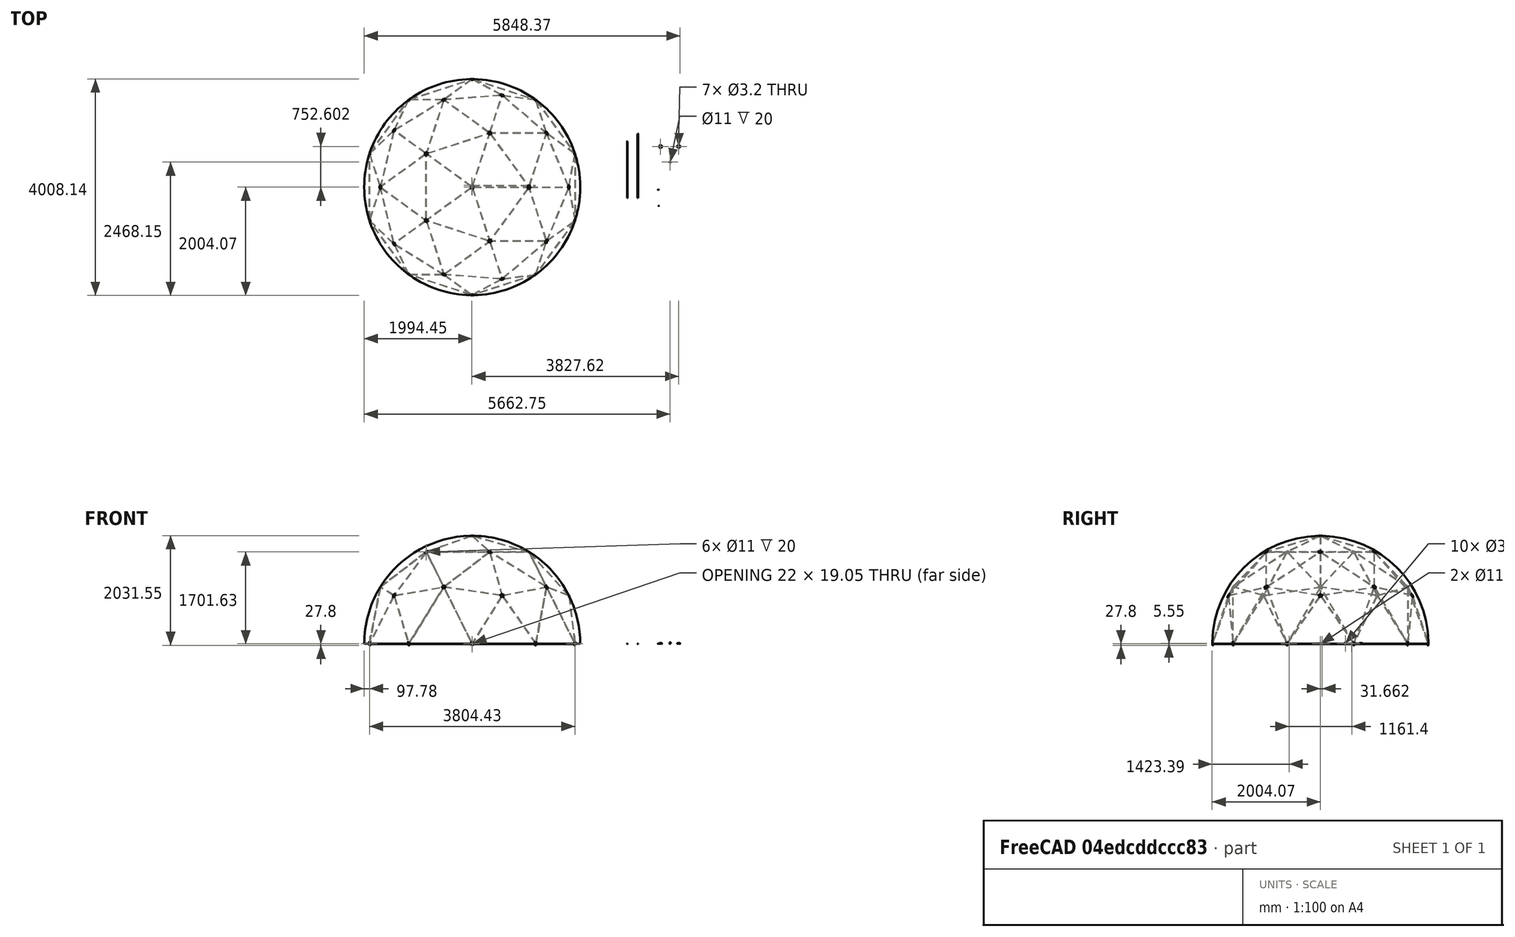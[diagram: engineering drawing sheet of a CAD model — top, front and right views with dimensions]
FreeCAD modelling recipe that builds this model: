
FCSTD DOCUMENT  (FreeCAD 0.20R29177 +233 (Git))
Label: 02-domo-3D
License: All rights reserved
LicenseURL: http://en.wikipedia.org/wiki/All_rights_reserved
objects: Part::Feature×235, Part::Part2DObjectPython×138, App::DocumentObjectGroup×21, App::Annotation×18, Part::Mirroring×7, App::FeaturePython×4, Part::Sphere×1, Part::Cylinder×1
note: 382 computed .brp shape members not serialized (recipe doc carries the construction recipe); baked Part::Feature solids carry a one-line shape summary decoded from their .brp

FEATURE [Part::Part2DObjectPython] Line  # Draft 2D object (typed FeaturePython)
  ChamferSize = 0
  Closed = false
  End = (-1902.16,617.998,0)
  FilletRadius = 0
  Length = 1236.1
  MakeFace = true
  MapMode = 5
  Placement = pos=(-1154.86,1595.54,0) rot=(0,0,-1;0.628319rad)
  Points = (2) [(-30,6,0),(-30,-1230.1,0)]
  Start = (-1175.6,1618.02,0)
  Subdivisions = 0
FEATURE [Part::Part2DObjectPython] Line003  # Draft 2D object (typed FeaturePython)
  ChamferSize = 0
  Closed = false
  End = (-1175.6,1618.02,0)
  FilletRadius = 0
  Length = 1236.1
  MakeFace = true
  MapMode = 5
  Placement = pos=(3.56417,1969.61,0) rot=(0,0,-1;1.25664rad)
  Points = (2) [(-30,6,0),(-30,-1230.1,0)]
  Start = (3.56741e-11,2000,0)
  Subdivisions = 0
FEATURE [Part::Mirroring] Part__Mirroring  label="Line (Mirror #1)"
  Base = (0,0,0)
  Normal = (1,0,0)
  Source = -> Line
FEATURE [Part::Mirroring] Part__Mirroring001  label="Line003 (Mirror #2)"
  Base = (0,0,0)
  Normal = (1,0,0)
  Source = -> Line003
FEATURE [Part::Mirroring] Part__Mirroring002  label="Line (Mirror #3)"
  Base = (0,0,0)
  Normal = (0,1,0)
  Source = -> Line
FEATURE [Part::Mirroring] Part__Mirroring003  label="Line003 (Mirror #4)"
  Base = (0,0,0)
  Normal = (0,1,0)
  Source = -> Line003
FEATURE [Part::Mirroring] Part__Mirroring004  label="Line (Mirror #5)"
  Base = (0,0,0)
  Normal = (0,1,0)
  Source = -> Part__Mirroring
FEATURE [Part::Mirroring] Part__Mirroring005  label="Line003 (Mirror #6)"
  Base = (0,0,0)
  Normal = (0,1,0)
  Source = -> Part__Mirroring001
FEATURE [Part::Part2DObjectPython] Line006  # Draft 2D object (typed FeaturePython)
  ChamferSize = 0
  Closed = false
  End = (-1902.16,-617.998,0)
  FilletRadius = 0
  Length = 1236
  MakeFace = true
  MapMode = 5
  Points = (2) [(-1902.16,617.998,0),(-1902.16,-617.998,0)]
  Start = (-1902.16,617.998,0)
  Subdivisions = 0
FEATURE [Part::Sphere] Sphere
  Angle1 = 0
  Angle2 = 90
  Angle3 = 360
  AttacherType = Attacher::AttachEngine3D
  Radius = 2000
FEATURE [Part::Part2DObjectPython] Line014  # Draft 2D object (typed FeaturePython)
  ChamferSize = 0
  Closed = false
  End = (1902.16,3e-10,0)
  FilletRadius = 0
  Length = 1902.16
  MakeFace = true
  MapMode = 5
  Points = (2) [(-1.99975e-10,3.00133e-10,0),(1902.16,3.0025e-10,0)]
  Start = (0,0,0)
  Subdivisions = 0
FEATURE [Part::Part2DObjectPython] Line015  # Draft 2D object (typed FeaturePython)
  ChamferSize = 0
  Closed = false
  End = (1902.16,3e-10,0)
  FilletRadius = 0
  Length = 1902.16
  MakeFace = true
  MapMode = 5
  Points = (2) [(-1.99975e-10,3.00133e-10,0),(1902.16,3.0025e-10,0)]
  Start = (0,0,0)
  Subdivisions = 0
FEATURE [Part::Part2DObjectPython] Line016  # Draft 2D object (typed FeaturePython)
  ChamferSize = 0
  Closed = false
  End = (587.785,1809.02,0)
  FilletRadius = 0
  Length = 1902.11
  MakeFace = true
  MapMode = 5
  Points = (2) [(-1.99975e-10,3.00133e-10,0),(587.785,1809.02,0)]
  Start = (0,0,0)
  Subdivisions = 0
FEATURE [Part::Part2DObjectPython] Line017  # Draft 2D object (typed FeaturePython)
  ChamferSize = 0
  Closed = false
  End = (-1538.86,1118.05,0)
  FilletRadius = 0
  Length = 1902.13
  MakeFace = true
  MapMode = 5
  Points = (2) [(-1.99975e-10,3.00133e-10,0),(-1538.86,1118.05,0)]
  Start = (0,0,0)
  Subdivisions = 0
FEATURE [Part::Part2DObjectPython] Line018  # Draft 2D object (typed FeaturePython)
  ChamferSize = 0
  Closed = false
  End = (-1538.86,-1118.05,0)
  FilletRadius = 0
  Length = 1902.13
  MakeFace = true
  MapMode = 5
  Points = (2) [(-1.99975e-10,3.00133e-10,0),(-1538.86,-1118.05,0)]
  Start = (0,0,0)
  Subdivisions = 0
FEATURE [Part::Part2DObjectPython] Line019  # Draft 2D object (typed FeaturePython)
  ChamferSize = 0
  Closed = false
  End = (-577.454,-703.099,0)
  FilletRadius = 0
  Length = 1093.1
  MakeFace = true
  MapMode = 5
  Placement = pos=(1075.61,-2380.95,0) rot=(0,0,-1;0.581932rad)
  Points = (2) [(-2300,-600,0),(-2303.19,493.095,0)]
  Start = (-1175.6,-1618.02,0)
  Subdivisions = 0
FEATURE [Part::Part2DObjectPython] Line022  # Draft 2D object (typed FeaturePython)
  ChamferSize = 0
  Closed = false
  End = (587.8,-1809.01,0)
  FilletRadius = 0
  Length = 1902.11
  MakeFace = true
  MapMode = 5
  Points = (2) [(-1.99975e-10,3.00133e-10,0),(587.8,-1809.01,0)]
  Start = (0,0,0)
  Subdivisions = 0
FEATURE [Part::Part2DObjectPython] Line023  # Draft 2D object (typed FeaturePython)
  ChamferSize = 0
  Closed = false
  End = (0,0,2000)
  FilletRadius = 0
  Length = 2000
  MakeFace = true
  MapMode = 5
  Points = (2) [(-1.99975e-10,3.00133e-10,0),(1.22465e-13,-2.99952e-29,2000)]
  Start = (0,0,0)
  Subdivisions = 0
FEATURE [Part::Part2DObjectPython] DWire001  # Draft 2D object (typed FeaturePython)
  ChamferSize = 0
  Closed = true
  End = (1902.16,617.998,0)
  FilletRadius = 0
  Length = 3422.2
  MakeFace = true
  MapMode = 5
  Points = (3) [(1902.16,-617.998,0),(1788.83,-9.64734e-10,894.484),(1902.16,617.998,0)]
  Start = (1902.16,-617.998,0)
  Subdivisions = 0
FEATURE [Part::Part2DObjectPython] DWire  # Draft 2D object (typed FeaturePython)
  ChamferSize = 0
  Closed = true
  End = (587.785,1809.02,0)
  FilletRadius = 0
  Length = 6662.19
  MakeFace = true
  MapMode = 5
  Points = (3) [(1.22465e-13,0,2000),(-1.99975e-10,3.00133e-10,0),(587.785,1809.02,0)]
  Start = (0,0,2000)
  Subdivisions = 0
FEATURE [Part::Mirroring] Part__Mirroring006  label="DWire003 (Mirror #7)"
  Base = (0,0,0)
  Normal = (0,1,0)
FEATURE [Part::Part2DObjectPython] Arc  # Draft 2D object (typed FeaturePython)
  FirstAngle = 56.8247
  LastAngle = 105.817
  MakeFace = true
  MapMode = 5
  Placement = pos=(-1175.6,-1618.02,0) rot=(0,0,1;0rad)
  Radius = 1093.1
FEATURE [Part::Part2DObjectPython] Line026  # Draft 2D object (typed FeaturePython)
  ChamferSize = 0
  Closed = false
  End = (-1902.16,-617.998,0)
  FilletRadius = 0
  Length = 1093.15
  MakeFace = true
  MapMode = 5
  Points = (2) [(-809.424,-588.081,0),(-1902.16,-617.998,0)]
  Start = (-809.424,-588.081,0)
  Subdivisions = 0
FEATURE [Part::Part2DObjectPython] DWire004  # Draft 2D object (typed FeaturePython)
  ChamferSize = 0
  Closed = true
  End = (-1538.86,-1118.05,0)
  FilletRadius = 0
  Length = 6662.22
  MakeFace = true
  MapMode = 5
  Points = (3) [(1.22465e-13,0,2000),(-1.99975e-10,3.00133e-10,0),(-1538.86,-1118.05,0)]
  Start = (0,0,2000)
  Subdivisions = 0
FEATURE [Part::Part2DObjectPython] DWire005  # Draft 2D object (typed FeaturePython)
  ChamferSize = 0
  Closed = true
  End = (-1175.6,-1618.02,0)
  FilletRadius = 0
  Length = 3422.35
  MakeFace = true
  MapMode = 5
  Points = (3) [(-1902.16,-617.998,0),(-1447.19,-1051.45,894.481),(-1175.6,-1618.02,0)]
  Start = (-1902.16,-617.998,0)
  Subdivisions = 0
FEATURE [Part::Part2DObjectPython] Line027  # Draft 2D object (typed FeaturePython)
  ChamferSize = 0
  Closed = false
  End = (-878.683,234.127,0)
  FilletRadius = 0
  Length = 1093.1
  MakeFace = true
  MapMode = 5
  Placement = pos=(-2154.97,-1745.49,0) rot=(0,0,-1;1.93254rad)
  Points = (2) [(-2300,-600,0),(-2303.19,493.095,0)]
  Start = (-1902.16,617.998,0)
  Subdivisions = 0
FEATURE [Part::Part2DObjectPython] Arc003  # Draft 2D object (typed FeaturePython)
  FirstAngle = -20.5593
  LastAngle = 28.7005
  MakeFace = true
  MapMode = 5
  Placement = pos=(-1902.16,617.998,0) rot=(0,0,1;0rad)
  Radius = 1093.1
FEATURE [Part::Part2DObjectPython] DWire006  # Draft 2D object (typed FeaturePython)
  ChamferSize = 0
  Closed = true
  End = (-1538.86,1118.05,0)
  FilletRadius = 0
  Length = 6662.22
  MakeFace = true
  MapMode = 5
  Points = (3) [(1.22465e-13,0,2000),(-1.99975e-10,3.00133e-10,0),(-1538.86,1118.05,0)]
  Start = (0,0,2000)
  Subdivisions = 0
FEATURE [Part::Part2DObjectPython] DWire007  # Draft 2D object (typed FeaturePython)
  ChamferSize = 0
  Closed = true
  End = (-1902.16,617.998,0)
  FilletRadius = 0
  Length = 3422.25
  MakeFace = true
  MapMode = 5
  Points = (3) [(-1175.6,1618.02,0),(-1447.21,1051.46,894.426),(-1902.16,617.998,0)]
  Start = (-1175.6,1618.02,0)
  Subdivisions = 0
FEATURE [Part::Part2DObjectPython] DWire008  # Draft 2D object (typed FeaturePython)
  ChamferSize = 0
  Closed = true
  End = (324.937,-1000.03,1701.28)
  FilletRadius = 0
  Length = 3422.31
  MakeFace = true
  MapMode = 5
  Points = (3) [(2.23523e-10,2.82703e-10,2000),(-850.675,-618.052,1701.28),(324.937,-1000.03,1701.28)]
  Start = (2.24e-10,2.83e-10,2000)
  Subdivisions = 0
FEATURE [Part::Part2DObjectPython] DWire009  # Draft 2D object (typed FeaturePython)
  ChamferSize = 0
  Closed = true
  End = (-2e-10,3e-10,2000)
  FilletRadius = 0
  Length = 3422.3
  MakeFace = true
  MapMode = 5
  Points = (3) [(324.937,-1000.03,1701.28),(1051.49,1.3321e-09,1701.28),(-1.99876e-10,3.00061e-10,2000)]
  Start = (324.937,-1000.03,1701.28)
  Subdivisions = 0
FEATURE [Part::Part2DObjectPython] DWire010  # Draft 2D object (typed FeaturePython)
  ChamferSize = 0
  Closed = true
  End = (324.929,1000.03,1701.28)
  FilletRadius = 0
  Length = 3422.3
  MakeFace = true
  MapMode = 5
  Points = (3) [(-1.99876e-10,3.00061e-10,2000),(1051.49,1.3321e-09,1701.28),(324.929,1000.03,1701.28)]
  Start = (-2e-10,3e-10,2000)
  Subdivisions = 0
FEATURE [Part::Part2DObjectPython] DWire011  # Draft 2D object (typed FeaturePython)
  ChamferSize = 0
  Closed = true
  End = (-850.675,618.052,1701.28)
  FilletRadius = 0
  Length = 3422.3
  MakeFace = true
  MapMode = 5
  Points = (3) [(-1.99876e-10,3.00061e-10,2000),(324.929,1000.03,1701.28),(-850.675,618.052,1701.28)]
  Start = (-2e-10,3e-10,2000)
  Subdivisions = 0
FEATURE [Part::Part2DObjectPython] DWire012  # Draft 2D object (typed FeaturePython)
  ChamferSize = 0
  Closed = true
  End = (-850.675,-618.052,1701.28)
  FilletRadius = 0
  Length = 3422.3
  MakeFace = true
  MapMode = 5
  Points = (3) [(-1.99876e-10,3.00061e-10,2000),(-850.675,618.052,1701.28),(-850.675,-618.052,1701.28)]
  Start = (-2e-10,3e-10,2000)
  Subdivisions = 0
FEATURE [Part::Part2DObjectPython] Line040  # Draft 2D object (typed FeaturePython)
  ChamferSize = 0
  Closed = false
  End = (-1447.19,-1051.45,894.481)
  FilletRadius = 0
  Length = 1092.97
  MakeFace = true
  MapMode = 5
  Points = (2) [(-850.675,-618.052,1701.28),(-1447.19,-1051.45,894.481)]
  Start = (-850.675,-618.052,1701.28)
  Subdivisions = 0
FEATURE [Part::Part2DObjectPython] DWire013  # Draft 2D object (typed FeaturePython)
  ChamferSize = 0
  Closed = true
  End = (0,0,2000)
  FilletRadius = 0
  Length = 6662.22
  MakeFace = true
  MapMode = 5
  Points = (3) [(1538.88,-1118.01,0),(-1.99975e-10,3.00133e-10,0),(1.22465e-13,0,2000)]
  Start = (1538.88,-1118.01,0)
  Subdivisions = 0
FEATURE [Part::Part2DObjectPython] Arc007  # Draft 2D object (typed FeaturePython)
  FirstAngle = -90
  LastAngle = 6.05971
  MakeFace = true
  MapMode = 5
  Placement = pos=(7.36405e-11,1.01362e-10,0) rot=(0.223911,0.689153,0.689153;2.70104rad)
  Radius = 2000
  Support = -> [DWire013]
FEATURE [Part::Part2DObjectPython] DWire014  # Draft 2D object (typed FeaturePython)
  ChamferSize = 0
  Closed = true
  End = (1902.16,-617.998,0)
  FilletRadius = 0
  Length = 3708.32
  MakeFace = true
  MapMode = 5
  Points = (3) [(1175.6,-1618.02,0),(1376.39,-999.957,1051.5),(1902.16,-617.998,0)]
  Start = (1175.6,-1618.02,0)
  Subdivisions = 0
FEATURE [Part::Part2DObjectPython] DWire015  # Draft 2D object (typed FeaturePython)
  ChamferSize = 0
  Closed = true
  End = (1051.49,1.332e-09,1701.28)
  FilletRadius = 0
  Length = 3708.12
  MakeFace = true
  MapMode = 5
  Points = (3) [(1376.39,-999.957,1051.5),(324.937,-1000.03,1701.28),(1051.49,1.3321e-09,1701.28)]
  Start = (1376.39,-999.957,1051.5)
  Subdivisions = 0
FEATURE [Part::Part2DObjectPython] DWire016  # Draft 2D object (typed FeaturePython)
  ChamferSize = 0
  Closed = true
  End = (1175.6,-1618.02,0)
  FilletRadius = 0
  Length = 3422.29
  MakeFace = true
  MapMode = 5
  Points = (3) [(552.796,-1701.28,894.456),(1376.39,-999.957,1051.5),(1175.6,-1618.02,0)]
  Start = (552.796,-1701.28,894.456)
  Subdivisions = 0
FEATURE [Part::Part2DObjectPython] DWire017  # Draft 2D object (typed FeaturePython)
  ChamferSize = 0
  Closed = true
  End = (1902.16,-617.998,0)
  FilletRadius = 0
  Length = 3422.23
  MakeFace = true
  MapMode = 5
  Points = (3) [(1376.39,-999.957,1051.5),(1788.83,-9.64734e-10,894.484),(1902.16,-617.998,0)]
  Start = (1376.39,-999.957,1051.5)
  Subdivisions = 0
FEATURE [Part::Part2DObjectPython] DWire018  # Draft 2D object (typed FeaturePython)
  ChamferSize = 0
  Closed = true
  End = (1376.39,-999.957,1051.5)
  FilletRadius = 0
  Length = 3422.11
  MakeFace = true
  MapMode = 5
  Points = (3) [(324.937,-1000.03,1701.28),(552.796,-1701.28,894.456),(1376.39,-999.957,1051.5)]
  Start = (324.937,-1000.03,1701.28)
  Subdivisions = 0
FEATURE [Part::Part2DObjectPython] DWire019  # Draft 2D object (typed FeaturePython)
  ChamferSize = 0
  Closed = true
  End = (1788.83,-9.65e-10,894.484)
  FilletRadius = 0
  Length = 3421.98
  MakeFace = true
  MapMode = 5
  Points = (3) [(1376.39,-999.957,1051.5),(1051.49,1.3321e-09,1701.28),(1788.83,-9.64734e-10,894.484)]
  Start = (1376.39,-999.957,1051.5)
  Subdivisions = 0
FEATURE [Part::Part2DObjectPython] DWire020  # Draft 2D object (typed FeaturePython)
  ChamferSize = 0
  Closed = true
  End = (1175.6,1618.02,0)
  FilletRadius = 0
  Length = 3708.32
  MakeFace = true
  MapMode = 5
  Points = (3) [(1902.16,617.998,0),(1376.39,999.957,1051.5),(1175.6,1618.02,0)]
  Start = (1902.16,617.998,0)
  Subdivisions = 0
FEATURE [Part::Part2DObjectPython] DWire021  # Draft 2D object (typed FeaturePython)
  ChamferSize = 0
  Closed = true
  End = (-1175.6,1618.02,0)
  FilletRadius = 0
  Length = 3708.32
  MakeFace = true
  MapMode = 5
  Points = (3) [(-525.738,1618.01,1051.5),(3.56977e-11,2000,0),(-1175.6,1618.02,0)]
  Start = (-525.738,1618.01,1051.5)
  Subdivisions = 0
FEATURE [Part::Part2DObjectPython] DWire022  # Draft 2D object (typed FeaturePython)
  ChamferSize = 0
  Closed = true
  End = (-1902.16,-617.998,0)
  FilletRadius = 0
  Length = 3708.18
  MakeFace = true
  MapMode = 5
  Points = (3) [(-1701.28,-1.02242e-09,1051.5),(-1902.16,617.998,0),(-1902.16,-617.998,0)]
  Start = (-1701.28,-1.022e-09,1051.5)
  Subdivisions = 0
FEATURE [Part::Part2DObjectPython] DWire023  # Draft 2D object (typed FeaturePython)
  ChamferSize = 0
  Closed = true
  End = (-3.6e-11,-2000,0)
  FilletRadius = 0
  Length = 3708.32
  MakeFace = true
  MapMode = 5
  Points = (3) [(-525.738,-1618.01,1051.5),(-1175.6,-1618.02,0),(-3.5925e-11,-2000,0)]
  Start = (-525.738,-1618.01,1051.5)
  Subdivisions = 0
FEATURE [Part::Part2DObjectPython] DWire024  # Draft 2D object (typed FeaturePython)
  ChamferSize = 0
  Closed = true
  End = (324.929,1000.03,1701.28)
  FilletRadius = 0
  Length = 3708.14
  MakeFace = true
  MapMode = 5
  Points = (3) [(1051.49,1.3321e-09,1701.28),(1376.39,999.957,1051.5),(324.929,1000.03,1701.28)]
  Start = (1051.49,1.332e-09,1701.28)
  Subdivisions = 0
FEATURE [Part::Part2DObjectPython] DWire025  # Draft 2D object (typed FeaturePython)
  ChamferSize = 0
  Closed = true
  End = (1376.39,999.957,1051.5)
  FilletRadius = 0
  Length = 3421.98
  MakeFace = true
  MapMode = 5
  Points = (3) [(1051.49,1.3321e-09,1701.28),(1788.83,-9.64734e-10,894.484),(1376.39,999.957,1051.5)]
  Start = (1051.49,1.332e-09,1701.28)
  Subdivisions = 0
FEATURE [Part::Part2DObjectPython] DWire026  # Draft 2D object (typed FeaturePython)
  ChamferSize = 0
  Closed = true
  End = (1376.39,999.957,1051.5)
  FilletRadius = 0
  Length = 3422.23
  MakeFace = true
  MapMode = 5
  Points = (3) [(1788.83,-9.64734e-10,894.484),(1902.16,617.998,0),(1376.39,999.957,1051.5)]
  Start = (1788.83,-9.65e-10,894.484)
  Subdivisions = 0
FEATURE [Part::Part2DObjectPython] DWire027  # Draft 2D object (typed FeaturePython)
  ChamferSize = 0
  Closed = true
  End = (552.796,1701.28,894.456)
  FilletRadius = 0
  Length = 3422.29
  MakeFace = true
  MapMode = 5
  Points = (3) [(1376.39,999.957,1051.5),(1175.6,1618.02,0),(552.796,1701.28,894.456)]
  Start = (1376.39,999.957,1051.5)
  Subdivisions = 0
FEATURE [Part::Part2DObjectPython] DWire028  # Draft 2D object (typed FeaturePython)
  ChamferSize = 0
  Closed = true
  End = (552.796,1701.28,894.456)
  FilletRadius = 0
  Length = 3422.12
  MakeFace = true
  MapMode = 5
  Points = (3) [(324.929,1000.03,1701.28),(1376.39,999.957,1051.5),(552.796,1701.28,894.456)]
  Start = (324.929,1000.03,1701.28)
  Subdivisions = 0
FEATURE [Part::Part2DObjectPython] DWire029  # Draft 2D object (typed FeaturePython)
  ChamferSize = 0
  Closed = true
  End = (-3.6e-11,2000,0)
  FilletRadius = 0
  Length = 3422.29
  MakeFace = true
  MapMode = 5
  Points = (3) [(-525.738,1618.01,1051.5),(552.796,1701.28,894.456),(-3.5925e-11,2000,0)]
  Start = (-525.738,1618.01,1051.5)
  Subdivisions = 0
FEATURE [Part::Part2DObjectPython] DWire030  # Draft 2D object (typed FeaturePython)
  ChamferSize = 0
  Closed = true
  End = (-525.738,1618.01,1051.5)
  FilletRadius = 0
  Length = 3422.11
  MakeFace = true
  MapMode = 5
  Points = (3) [(324.929,1000.03,1701.28),(552.796,1701.28,894.456),(-525.738,1618.01,1051.5)]
  Start = (324.929,1000.03,1701.28)
  Subdivisions = 0
FEATURE [Part::Part2DObjectPython] DWire031  # Draft 2D object (typed FeaturePython)
  ChamferSize = 0
  Closed = true
  End = (-850.675,618.052,1701.28)
  FilletRadius = 0
  Length = 3708.14
  MakeFace = true
  MapMode = 5
  Points = (3) [(324.929,1000.03,1701.28),(-525.738,1618.01,1051.5),(-850.675,618.052,1701.28)]
  Start = (324.929,1000.03,1701.28)
  Subdivisions = 0
FEATURE [Part::Part2DObjectPython] DWire032  # Draft 2D object (typed FeaturePython)
  ChamferSize = 0
  Closed = true
  End = (-1447.21,1051.46,894.426)
  FilletRadius = 0
  Length = 3422.21
  MakeFace = true
  MapMode = 5
  Points = (3) [(-525.738,1618.01,1051.5),(-1175.6,1618.02,0),(-1447.21,1051.46,894.426)]
  Start = (-525.738,1618.01,1051.5)
  Subdivisions = 0
FEATURE [Part::Part2DObjectPython] DWire033  # Draft 2D object (typed FeaturePython)
  ChamferSize = 0
  Closed = true
  End = (-1447.21,1051.46,894.426)
  FilletRadius = 0
  Length = 3422.1
  MakeFace = true
  MapMode = 5
  Points = (3) [(-525.738,1618.01,1051.5),(-850.675,618.052,1701.28),(-1447.21,1051.46,894.426)]
  Start = (-525.738,1618.01,1051.5)
  Subdivisions = 0
FEATURE [Part::Part2DObjectPython] DWire034  # Draft 2D object (typed FeaturePython)
  ChamferSize = 0
  Closed = true
  End = (-1701.28,-1.022e-09,1051.5)
  FilletRadius = 0
  Length = 3422.12
  MakeFace = true
  MapMode = 5
  Points = (3) [(-850.675,618.052,1701.28),(-1447.21,1051.46,894.426),(-1701.28,-1.02242e-09,1051.5)]
  Start = (-850.675,618.052,1701.28)
  Subdivisions = 0
FEATURE [Part::Part2DObjectPython] DWire035  # Draft 2D object (typed FeaturePython)
  ChamferSize = 0
  Closed = true
  End = (-1701.28,-1.022e-09,1051.5)
  FilletRadius = 0
  Length = 3422.26
  MakeFace = true
  MapMode = 5
  Points = (3) [(-1447.21,1051.46,894.426),(-1902.16,617.998,0),(-1701.28,-1.02242e-09,1051.5)]
  Start = (-1447.21,1051.46,894.426)
  Subdivisions = 0
FEATURE [Part::Part2DObjectPython] DWire036  # Draft 2D object (typed FeaturePython)
  ChamferSize = 0
  Closed = true
  End = (-850.675,-618.052,1701.28)
  FilletRadius = 0
  Length = 3708.14
  MakeFace = true
  MapMode = 5
  Points = (3) [(-850.675,618.052,1701.28),(-1701.28,-1.02242e-09,1051.5),(-850.675,-618.052,1701.28)]
  Start = (-850.675,618.052,1701.28)
  Subdivisions = 0
FEATURE [Part::Part2DObjectPython] DWire037  # Draft 2D object (typed FeaturePython)
  ChamferSize = 0
  Closed = true
  End = (-1447.19,-1051.45,894.481)
  FilletRadius = 0
  Length = 3422.04
  MakeFace = true
  MapMode = 5
  Points = (3) [(-1701.28,-1.02242e-09,1051.5),(-850.675,-618.052,1701.28),(-1447.19,-1051.45,894.481)]
  Start = (-1701.28,-1.022e-09,1051.5)
  Subdivisions = 0
FEATURE [Part::Part2DObjectPython] DWire038  # Draft 2D object (typed FeaturePython)
  ChamferSize = 0
  Closed = true
  End = (-1447.19,-1051.45,894.481)
  FilletRadius = 0
  Length = 3422.29
  MakeFace = true
  MapMode = 5
  Points = (3) [(-1701.28,-1.02242e-09,1051.5),(-1902.16,-617.998,0),(-1447.19,-1051.45,894.481)]
  Start = (-1701.28,-1.022e-09,1051.5)
  Subdivisions = 0
FEATURE [Part::Part2DObjectPython] DWire039  # Draft 2D object (typed FeaturePython)
  ChamferSize = 0
  Closed = true
  End = (-525.738,-1618.01,1051.5)
  FilletRadius = 0
  Length = 3422.02
  MakeFace = true
  MapMode = 5
  Points = (3) [(-850.675,-618.052,1701.28),(-1447.19,-1051.45,894.481),(-525.738,-1618.01,1051.5)]
  Start = (-850.675,-618.052,1701.28)
  Subdivisions = 0
FEATURE [Part::Part2DObjectPython] DWire040  # Draft 2D object (typed FeaturePython)
  ChamferSize = 0
  Closed = true
  End = (324.937,-1000.03,1701.28)
  FilletRadius = 0
  Length = 3708.15
  MakeFace = true
  MapMode = 5
  Points = (3) [(-850.675,-618.052,1701.28),(-525.738,-1618.01,1051.5),(324.937,-1000.03,1701.28)]
  Start = (-850.675,-618.052,1701.28)
  Subdivisions = 0
FEATURE [Part::Part2DObjectPython] DWire041  # Draft 2D object (typed FeaturePython)
  ChamferSize = 0
  Closed = true
  End = (-1447.19,-1051.45,894.481)
  FilletRadius = 0
  Length = 3422.24
  MakeFace = true
  MapMode = 5
  Points = (3) [(-525.738,-1618.01,1051.5),(-1175.6,-1618.02,0),(-1447.19,-1051.45,894.481)]
  Start = (-525.738,-1618.01,1051.5)
  Subdivisions = 0
FEATURE [Part::Part2DObjectPython] DWire042  # Draft 2D object (typed FeaturePython)
  ChamferSize = 0
  Closed = true
  End = (552.796,-1701.28,894.456)
  FilletRadius = 0
  Length = 3422.12
  MakeFace = true
  MapMode = 5
  Points = (3) [(-525.738,-1618.01,1051.5),(324.937,-1000.03,1701.28),(552.796,-1701.28,894.456)]
  Start = (-525.738,-1618.01,1051.5)
  Subdivisions = 0
FEATURE [Part::Part2DObjectPython] DWire043  # Draft 2D object (typed FeaturePython)
  ChamferSize = 0
  Closed = true
  End = (552.796,-1701.28,894.456)
  FilletRadius = 0
  Length = 3422.29
  MakeFace = true
  MapMode = 5
  Points = (3) [(-525.738,-1618.01,1051.5),(-3.5925e-11,-2000,0),(552.796,-1701.28,894.456)]
  Start = (-525.738,-1618.01,1051.5)
  Subdivisions = 0
FEATURE [App::DocumentObjectGroup] Group001  label="Top-pentagon"
  Group = -> [DWire010,DWire011,DWire012,DWire008,DWire009]
FEATURE [App::DocumentObjectGroup] Group002  label="Pentagon-1"
  Group = -> [DWire019,DWire025,DWire026,DWire001,DWire017]
FEATURE [App::DocumentObjectGroup] Group003  label="Pentagon-2"
  Group = -> [DWire028,DWire030,DWire029,Part__Mirroring006,DWire027]
FEATURE [App::DocumentObjectGroup] Group004  label="Pentagon-3"
  Group = -> [DWire033,DWire034,DWire035,DWire007,DWire032]
FEATURE [App::DocumentObjectGroup] Group005  label="Pentagon-4"
  Group = -> [DWire037,DWire038,DWire005,DWire041,Line040,DWire039]
FEATURE [Part::Part2DObjectPython] DWire044  # Draft 2D object (typed FeaturePython)
  ChamferSize = 0
  Closed = true
  End = (1175.6,-1618.02,0)
  FilletRadius = 0
  Length = 3422.3
  MakeFace = true
  MapMode = 5
  Points = (3) [(-3.5925e-11,-2000,0),(552.796,-1701.28,894.456),(1175.6,-1618.02,0)]
  Start = (-3.6e-11,-2000,0)
  Subdivisions = 0
FEATURE [App::DocumentObjectGroup] Group006  label="Pentagon-5"
  Group = -> [DWire042,DWire043,DWire016,DWire018,DWire044]
FEATURE [App::DocumentObjectGroup] Group007  label="Aux"
  Group = -> [Part__Mirroring002,Part__Mirroring003,Part__Mirroring004,Part__Mirroring005,Line006,Line014,Line015,Line016,Line017,Line018,Line019,Line022,Line023,DWire,Arc,Line026,DWire004,Line027,Arc003,DWire006,DWire013,Arc007,Sphere]
FEATURE [Part::Part2DObjectPython] DWire045  label="Bottom"  # Draft 2D object (typed FeaturePython)
  ChamferSize = 0
  Closed = true
  End = (1902.16,-617.998,0)
  FilletRadius = 0
  Length = 12360.8
  MakeFace = true
  MapMode = 5
  Points = (10) [(1902.16,617.998,0),(1175.6,1618.02,0),(3.56977e-11,2000,0),(-1175.6,1618.02,0),(-1902.16,617.998,0),(-1902.16,-617.998,0),(-1175.6,-1618.02,0),+3 more]
  Start = (1902.16,617.998,0)
  Subdivisions = 0
FEATURE [App::DocumentObjectGroup] Group008  label="Green-triangles"
  Group = -> [DWire023,DWire040,DWire015,DWire014,DWire024,DWire031,DWire036,DWire022,DWire021,DWire020]
FEATURE [Part::Feature] Clone002  label="Hub-007"
  Placement = pos=(1044.95,2.82704e-10,1690.69) rot=(0.191324,0.71403,0.673466;0.757331rad)
  shape: bbox 49.68 x 55.6 x 37.22 mm, 28 faces (baked)
FEATURE [Part::Feature] Clone005  label="strutcap004"
  Placement = pos=(1066.92,2.82878e-10,1684.4) rot=(0.932253,0,0.361806;3.14159rad)
  shape: bbox 31.1 x 20 x 29.82 mm, 19 faces (baked)
FEATURE [Part::Feature] Clone008  label="strutcap007"
  Placement = pos=(1038.85,-19.0526,1701.75) rot=(0.667656,-0.64473,0.372235;1.42598rad)
  shape: bbox 25.29 x 31.07 x 25.73 mm, 19 faces (baked)
FEATURE [Part::Feature] Clone009  label="strutcap008"
  Placement = pos=(1029.49,2.82532e-10,1707.53) rot=(0,-1,0;1.294rad)
  shape: bbox 31.29 x 20 x 25.37 mm, 19 faces (baked)
FEATURE [Part::Feature] Clone028  label="strutcap025"
  Placement = pos=(1902.2,-594.877,0) rot=(-1,-1.4e-05,1.4e-05;1.5708rad)
  shape: bbox 20.3 x 30 x 20 mm, 19 faces (baked)
FEATURE [Part::Feature] Clone030  label="strutcap027"
  Placement = pos=(1888.76,-636.496,-2.5e-14) rot=(0.909046,-0.294649,-0.294649;1.66601rad)
  shape: bbox 27.81 x 32.24 x 20 mm, 19 faces (baked)
FEATURE [Part::Feature] Clone031  label="Hub-012"
  Placement = pos=(1889.5,-613.884,-5e-15) rot=(0.154555,0.97582,-0.154555;1.59527rad)
  shape: bbox 27.47 x 52.09 x 55.6 mm, 28 faces (baked)
FEATURE [Part::Feature] Cylinder014  label="Varilla-B-modif-003"
  Placement = pos=(1902.16,593.953,-2.89e-13) rot=(1,1.4e-05,1.4e-05;1.5708rad)
  shape: bbox 10.03 x 1189 x 10 mm, 3 faces (baked)
FEATURE [App::DocumentObjectGroup] Group012
FEATURE [App::DocumentObjectGroup] Group  label="Domo-superficies"
  Group = -> [Group001,Group002,Group003,Group004,Group005,Group006,Group008,DWire045,Group012]
FEATURE [Part::Feature] Clone001004  label="Hub5-01-clave002"
  Placement = pos=(-1.81309e-05,2.82703e-10,1987.55) rot=(0,0,-1;0.314151rad)
  shape: bbox 54.38 x 55.6 x 12.4 mm, 25 faces (baked)
FEATURE [Part::Feature] Clone  label="strutcap031"
  Placement = pos=(22.0001,2.82694e-10,1993.75) rot=(0.797896,0,0.602796;3.14159rad)
  shape: bbox 32.05 x 20 x 22.68 mm, 19 faces (baked)
FEATURE [Part::Feature] Clone001005  label="Hub5-01-clave003"
  Placement = pos=(1777.69,2.82703e-10,888.915) rot=(0.523905,0.082976,0.847726;2.87466rad)
  shape: bbox 33.84 x 55.6 x 51.33 mm, 25 faces (baked)
FEATURE [Part::Feature] Clone001006  label="strutcap032"
  Placement = pos=(1773.4,2.82716e-10,911.365) rot=(0,-1,0;0.740475rad)
  shape: bbox 29.03 x 20 x 31.71 mm, 19 faces (baked)
FEATURE [Part::Feature] Clone001007  label="Hub-014"
  Placement = pos=(1889.5,613.885,-5e-15) rot=(-0.154531,0.975828,0.154531;1.59526rad)
  shape: bbox 27.47 x 52.09 x 55.6 mm, 28 faces (baked)
FEATURE [Part::Feature] Clone001008  label="strutcap033"
  Placement = pos=(1902.19,595.158,-2.5e-14) rot=(1,0.00069,0.00069;1.5708rad)
  shape: bbox 20.33 x 30.01 x 20 mm, 19 faces (baked)
FEATURE [Part::Feature] Clone001009  label="strutcap034"
  Placement = pos=(1888.6,636.724,0) rot=(-0.908667,-0.295233,0.295233;1.66643rad)
  shape: bbox 27.82 x 32.23 x 20 mm, 19 faces (baked)
FEATURE [Part::Feature] Clone001010  label="strutcap035"
  Placement = pos=(1899.8,-604.923,18.9221) rot=(-0.98127,-0.136231,0.136202;0.618302rad)
  shape: bbox 20 x 28.03 x 30.96 mm, 19 faces (baked)
FEATURE [Part::Feature] Clone001012  label="strutcap037"
  Placement = pos=(1791.2,-12.9311,875.769) rot=(0.998074,0.043631,0.044104;2.5353rad)
  shape: bbox 22.47 x 27.49 x 30.68 mm, 19 faces (baked)
FEATURE [Part::Cylinder] Cylinder015  label="Cylinder084"
  Angle = 360
  AttacherType = Attacher::AttachEngine3D
  FirstAngle = 0
  Height = 1047.11
  Placement = pos=(1066.92,2.82853e-10,1684.4) rot=(0.681894,-0.681894,0.264655;3.65904rad)
  Radius = 5
  SecondAngle = 0
FEATURE [Part::Feature] Cylinder016  label="Cylinder001"
  Placement = pos=(1791.23,-12.9283,875.771) rot=(0.998113,0.043415,0.043415;2.53525rad)
  shape: bbox 118.5 x 600.2 x 862.6 mm, 3 faces (baked)
FEATURE [Part::Feature] Clone001013  label="strutcap038"
  Placement = pos=(1791.12,13.8918,876.408) rot=(0.993179,0.082001,0.082896;3.73273rad)
  shape: bbox 22.73 x 28.03 x 30.67 mm, 19 faces (baked)
FEATURE [Part::Feature] Cylinder017  label="Cylinder002"
  Placement = pos=(1791.15,13.8946,876.414) rot=(0.993219,0.08221,0.08221;3.73262rad)
  shape: bbox 118.5 x 600.7 x 862.3 mm, 3 faces (baked)
FEATURE [Part::Feature] Clone001014  label="strutcap039"
  Placement = pos=(1899.68,606.357,19.8831) rot=(0.934186,-0.252314,0.25226;0.634069rad)
  shape: bbox 20 x 27.5 x 31.62 mm, 19 faces (baked)
FEATURE [Part::Feature] Cylinder018  label="Cylinder003"
  Placement = pos=(22.0001,2.82669e-10,1993.75) rot=(-0.623692,0.623692,-0.471188;2.26093rad)
  shape: bbox 1010 x 10 x 295.8 mm, 3 faces (baked)
FEATURE [Part::Feature] Cylinder019  label="Cylinder004"
  Placement = pos=(6.79821,20.9234,1993.75) rot=(-0.980863,0.155349,-0.117363;1.86613rad)
  shape: bbox 320.8 x 962 x 295.8 mm, 3 faces (baked)
FEATURE [Part::Feature] Clone001015  label="strutcap040"
  Placement = pos=(6.79821,20.9234,1993.75) rot=(0.690291,0.501531,0.521503;3.86596rad)
  shape: bbox 23.54 x 32.47 x 22.68 mm, 19 faces (baked)
FEATURE [Part::Feature] Clone001016  label="strutcap041"
  Placement = pos=(318.122,979.108,1707.53) rot=(0.463915,-0.638519,0.614065;1.73821rad)
  shape: bbox 23.11 x 31.33 x 25.37 mm, 19 faces (baked)
FEATURE [Part::Feature] Clone001018  label="Hub-015"
  Placement = pos=(322.898,993.806,1690.69) rot=(-0.123041,0.320528,0.939214;1.84115rad)
  shape: bbox 55.11 x 51.63 x 37.22 mm, 28 faces (baked)
FEATURE [Part::Feature] Clone001020  label="strutcap044"
  Placement = pos=(339.134,982.12,1701.75) rot=(0.773329,-0.182879,0.607056;2.21695rad)
  shape: bbox 29.76 x 30.45 x 20.75 mm, 19 faces (baked)
FEATURE [Part::Feature] Clone007  label="strutcap006"
  Placement = pos=(1038.85,19.0526,1701.75) rot=(-0.64113,-0.730539,-0.235086;1.6431rad)
  shape: bbox 27.52 x 31.98 x 20.74 mm, 19 faces (baked)
FEATURE [Part::Feature] Cylinder020  label="Varilla-B-modif-004"
  Placement = pos=(340.068,980.833,1701.75) rot=(0.90866,0.295244,0.295244;1.66644rad)
  shape: bbox 706.9 x 967.7 x 10 mm, 3 faces (baked)
FEATURE [Part::Feature] Clone001023  label="Hub-016"
  Placement = pos=(1367.83,993.738,1044.94) rot=(0.480375,0.156077,0.863064;3.68838rad)
  shape: bbox 46.36 x 51.63 x 50.11 mm, 28 faces (baked)
FEATURE [Part::Feature] Clone001027  label="strutcap049"
  Placement = pos=(1385.02,979.037,1048.2) rot=(0.929901,-0.068235,0.361425;1.8922rad)
  shape: bbox 27.6 x 31.33 x 20.3 mm, 19 faces (baked)
FEATURE [Part::Feature] Clone001030  label="strutcap052"
  Placement = pos=(1779.91,20.6545,898.82) rot=(-0.909103,-0.414228,-0.044114;1.42856rad)
  shape: bbox 24.46 x 32.53 x 22.38 mm, 19 faces (baked)
FEATURE [Part::Feature] Cylinder021  label="Cylinder005"
  Placement = pos=(1779.94,20.6643,898.834) rot=(-0.908834,-0.414887,-0.043473;1.42913rad)
  shape: bbox 403.8 x 962.4 x 159.4 mm, 3 faces (baked)
FEATURE [Part::Feature] Clone001031  label="strutcap053"
  Placement = pos=(1780.84,-21.3342,896.949) rot=(0.871498,-0.474485,0.123916;1.43836rad)
  shape: bbox 24.48 x 32.39 x 22.88 mm, 19 faces (baked)
FEATURE [Part::Feature] Cylinder022  label="Cylinder006"
  Placement = pos=(1780.87,-21.342,896.969) rot=(0.871257,-0.475095,0.123269;1.43902rad)
  shape: bbox 404.7 x 961.7 x 161.3 mm, 3 faces (baked)
FEATURE [Part::Feature] Clone001032  label="strutcap054"
  Placement = pos=(1385.02,-979.035,1048.21) rot=(-0.930319,-0.067054,-0.360569;1.89034rad)
  shape: bbox 27.6 x 31.33 x 20.29 mm, 19 faces (baked)
FEATURE [Part::Feature] Clone001033  label="Hub-017"
  Placement = pos=(1367.82,-993.731,1044.96) rot=(0.270395,0.832171,-0.484126;1.1821rad)
  shape: bbox 46.31 x 51.62 x 50.16 mm, 28 faces (baked)
FEATURE [Part::Feature] Clone001036  label="strutcap057"
  Placement = pos=(1359.16,-1014.63,1048.21) rot=(0.830217,-0.556143,-0.038018;1.57228rad)
  shape: bbox 27.82 x 32.54 x 20 mm, 19 faces (baked)
FEATURE [Part::Feature] Clone001037  label="strutcap058"
  Placement = pos=(1373.71,-1011.61,1031.99) rot=(0.909326,-0.37369,0.182983;2.49398rad)
  shape: bbox 21.91 x 31.15 x 29.81 mm, 19 faces (baked)
FEATURE [Part::Feature] Clone001038  label="strutcap059"
  Placement = pos=(1386.64,-993.808,1031.99) rot=(0.962095,-0.192679,0.192997;3.57034rad)
  shape: bbox 28.43 x 23.66 x 30.86 mm, 19 faces (baked)
FEATURE [Part::Part2DObjectPython] Line054  # Draft 2D object (typed FeaturePython)
  ChamferSize = 0
  Closed = false
  End = (1902.16,-617.998,0)
  FilletRadius = 0
  Length = 1236.1
  MakeFace = true
  MapMode = 5
  Points = (2) [(1175.6,-1618.02,0),(1902.16,-617.998,0)]
  Start = (1175.6,-1618.02,0)
  Subdivisions = 0
FEATURE [Part::Part2DObjectPython] Line055  # Draft 2D object (typed FeaturePython)
  ChamferSize = 0
  Closed = false
  End = (1902.16,617.998,0)
  FilletRadius = 0
  Length = 1236
  MakeFace = true
  MapMode = 5
  Points = (2) [(1902.16,-617.998,0),(1902.16,617.998,0)]
  Start = (1902.16,-617.998,0)
  Subdivisions = 0
FEATURE [Part::Part2DObjectPython] Line056  # Draft 2D object (typed FeaturePython)
  ChamferSize = 0
  Closed = false
  End = (1376.39,-999.957,1051.5)
  FilletRadius = 0
  Length = 1236
  MakeFace = true
  MapMode = 5
  Points = (2) [(1051.49,1.3321e-09,1701.28),(1376.39,-999.957,1051.5)]
  Start = (1051.49,1.332e-09,1701.28)
  Subdivisions = 0
FEATURE [Part::Part2DObjectPython] Line057  # Draft 2D object (typed FeaturePython)
  ChamferSize = 0
  Closed = false
  End = (1902.16,-617.998,0)
  FilletRadius = 0
  Length = 1236.11
  MakeFace = true
  MapMode = 5
  Points = (2) [(1376.39,-999.957,1051.5),(1902.16,-617.998,0)]
  Start = (1376.39,-999.957,1051.5)
  Subdivisions = 0
FEATURE [Part::Part2DObjectPython] Line058  # Draft 2D object (typed FeaturePython)
  ChamferSize = 0
  Closed = false
  End = (1376.39,999.957,1051.5)
  FilletRadius = 0
  Length = 1236
  MakeFace = true
  MapMode = 5
  Points = (2) [(1051.49,1.3321e-09,1701.28),(1376.39,999.957,1051.5)]
  Start = (1051.49,1.332e-09,1701.28)
  Subdivisions = 0
FEATURE [Part::Part2DObjectPython] Line059  # Draft 2D object (typed FeaturePython)
  ChamferSize = 0
  Closed = false
  End = (1902.16,617.998,0)
  FilletRadius = 0
  Length = 1236.11
  MakeFace = true
  MapMode = 5
  Points = (2) [(1376.39,999.957,1051.5),(1902.16,617.998,0)]
  Start = (1376.39,999.957,1051.5)
  Subdivisions = 0
FEATURE [Part::Feature] Cylinder023  label="Varilla-B-modif-005"
  Placement = pos=(1891.94,625.428,20.4541) rot=(-0.256517,-0.683428,-0.683465;0.767356rad)
  shape: bbox 514.7 x 376.8 x 1017 mm, 3 faces (baked)
FEATURE [Part::Feature] Clone001039  label="strutcap060"
  Placement = pos=(1386.87,993.248,1032.31) rot=(0.963511,0.189033,0.189506;2.73838rad)
  shape: bbox 28.28 x 23.32 x 30.96 mm, 19 faces (baked)
FEATURE [Part::Feature] Clone001040  label="strutcap061"
  Placement = pos=(1892,626.262,19.0526) rot=(-0.586671,-0.615427,0.526371;0.557536rad)
  shape: bbox 24.41 x 24.08 x 32.46 mm, 19 faces (baked)
FEATURE [Part::Feature] Clone001041  label="strutcap062"
  Placement = pos=(1370.43,982.035,1064.4) rot=(0.652966,-0.542424,0.528594;1.20781rad)
  shape: bbox 22.88 x 30.45 x 29.86 mm, 19 faces (baked)
FEATURE [Part::Feature] Cylinder024  label="Varilla-B-modif-006"
  Placement = pos=(1057.35,20.059,1689.56) rot=(0.887762,0.32548,0.325486;3.92675rad)
  shape: bbox 322.6 x 967 x 634.3 mm, 3 faces (baked)
FEATURE [Part::Feature] Clone001042  label="strutcap063"
  Placement = pos=(1057.34,19.1988,1690.32) rot=(0.882765,0.34052,0.323687;3.95983rad)
  shape: bbox 24.7 x 32.04 x 26.61 mm, 19 faces (baked)
FEATURE [Part::Feature] Cylinder025  label="Varilla-B-modif-007"
  Placement = pos=(1386.68,-992.502,1030.9) rot=(0.93165,0.256925,0.256939;3.33301rad)
  shape: bbox 514.9 x 375.8 x 1017 mm, 3 faces (baked)
FEATURE [Part::Feature] Clone001043  label="strutcap064"
  Placement = pos=(1892.07,-626.034,19.189) rot=(0.64134,-0.542546,-0.542518;0.709896rad)
  shape: bbox 25.5 x 26.02 x 32.03 mm, 19 faces (baked)
FEATURE [Part::Feature] Clone001044  label="strutcap065"
  Placement = pos=(1370.47,-982.061,1064.43) rot=(-0.67332,-0.525087,-0.520503;1.20241rad)
  shape: bbox 22.54 x 30.53 x 29.82 mm, 19 faces (baked)
FEATURE [Part::Feature] Clone001045  label="strutcap066"
  Placement = pos=(1057.56,-19.0526,1690.18) rot=(0.887841,-0.325204,0.325548;2.35642rad)
  shape: bbox 25.29 x 31.82 x 26.9 mm, 19 faces (baked)
FEATURE [Part::Feature] Cylinder027  label="Varilla-B-modif-009"
  Placement = pos=(1370.47,-982.061,1064.43) rot=(-0.669151,-0.525446,-0.525494;1.2188rad)
  shape: bbox 322.1 x 967.7 x 633.5 mm, 3 faces (baked)
FEATURE [Part::Part2DObjectPython] Line060  # Draft 2D object (typed FeaturePython)
  ChamferSize = 0
  Closed = false
  End = (324.929,1000.03,1701.28)
  FilletRadius = 0
  Length = 1236.1
  MakeFace = true
  MapMode = 5
  Points = (2) [(-850.675,618.052,1701.28),(324.929,1000.03,1701.28)]
  Start = (-850.675,618.052,1701.28)
  Subdivisions = 0
FEATURE [Part::Feature] Clone001047  label="strutcap068"
  Placement = pos=(302.894,993.894,1701.75) rot=(-0.095426,-0.931982,0.349719;1.72702rad)
  shape: bbox 31.97 x 22.84 x 20.72 mm, 19 faces (baked)
FEATURE [Part::Feature] Clone001049  label="strutcap070"
  Placement = pos=(-17.7986,12.9312,1993.75) rot=(-0.300922,-0.926155,-0.227341;1.92055rad)
  shape: bbox 31.35 x 28.31 x 22.68 mm, 19 faces (baked)
FEATURE [Part::Feature] Cylinder  label="Cylinder007"
  Placement = pos=(-17.7986,12.9312,1993.75) rot=(-0.842809,-0.429437,0.324432;2.00762rad)
  shape: bbox 821.2 x 600.3 x 295.8 mm, 3 faces (baked)
FEATURE [Part::Feature] Clone001050  label="Hub-018"
  Placement = pos=(-845.385,614.197,1690.69) rot=(-0.229479,0.149024,0.961837;3.04087rad)
  shape: bbox 52.89 x 52.48 x 37.22 mm, 28 faces (baked)
FEATURE [Part::Feature] Clone001051  label="strutcap071"
  Placement = pos=(-832.882,605.113,1707.53) rot=(0.591556,-0.192206,0.783019;2.64333rad)
  shape: bbox 30.27 x 27.49 x 25.37 mm, 19 faces (baked)
FEATURE [Part::Feature] Clone001052  label="strutcap072"
  Placement = pos=(-829.253,626.027,1701.75) rot=(0.656731,0.274649,0.702334;3.0586rad)
  shape: bbox 31.36 x 25.66 x 20.75 mm, 19 faces (baked)
FEATURE [Part::Feature] Clone001053  label="strutcap073"
  Placement = pos=(-844.393,637.027,1690.18) rot=(0.558841,0.681764,0.472117;3.47389rad)
  shape: bbox 22.99 x 32.33 x 26.68 mm, 19 faces (baked)
FEATURE [Part::Feature] Clone001054  label="strutcap074"
  Placement = pos=(-863.162,627.113,1684.4) rot=(0.306814,0.944291,0.119074;3.84415rad)
  shape: bbox 29.74 x 26.84 x 29.82 mm, 19 faces (baked)
FEATURE [Part::Feature] Clone001055  label="strutcap075"
  Placement = pos=(-866.791,606.199,1690.18) rot=(-0.037385,0.949845,-0.310478;3.97036rad)
  shape: bbox 31.57 x 26.83 x 26.72 mm, 19 faces (baked)
FEATURE [Part::Feature] Clone001056  label="strutcap076"
  Placement = pos=(-851.651,595.199,1701.75) rot=(-0.384951,0.662639,-0.642435;3.89838rad)
  shape: bbox 20.26 x 30.22 x 20.72 mm, 19 faces (baked)
FEATURE [Part::Feature] Cylinder028  label="Varilla-B-modif-010"
  Placement = pos=(-827.741,626.518,1701.75) rot=(0.456965,0.628961,0.628961;2.28433rad)
  shape: bbox 1134 x 376.9 x 10 mm, 3 faces (baked)
FEATURE [Part::Part2DObjectPython] Line061  # Draft 2D object (typed FeaturePython)
  ChamferSize = 0
  Closed = false
  End = (-850.675,-618.052,1701.28)
  FilletRadius = 0
  Length = 1236.1
  MakeFace = true
  MapMode = 5
  Points = (2) [(-850.675,618.052,1701.28),(-850.675,-618.052,1701.28)]
  Start = (-850.675,618.052,1701.28)
  Subdivisions = 0
FEATURE [Part::Part2DObjectPython] Line062  # Draft 2D object (typed FeaturePython)
  ChamferSize = 0
  Closed = false
  End = (324.937,-1000.03,1701.28)
  FilletRadius = 0
  Length = 1236.11
  MakeFace = true
  MapMode = 5
  Points = (2) [(-850.675,-618.052,1701.28),(324.937,-1000.03,1701.28)]
  Start = (-850.675,-618.052,1701.28)
  Subdivisions = 0
FEATURE [Part::Part2DObjectPython] Line063  # Draft 2D object (typed FeaturePython)
  ChamferSize = 0
  Closed = false
  End = (1051.49,1.332e-09,1701.28)
  FilletRadius = 0
  Length = 1236.1
  MakeFace = true
  MapMode = 5
  Points = (2) [(324.929,1000.03,1701.28),(1051.49,1.3321e-09,1701.28)]
  Start = (324.929,1000.03,1701.28)
  Subdivisions = 0
FEATURE [Part::Part2DObjectPython] Line064  # Draft 2D object (typed FeaturePython)
  ChamferSize = 0
  Closed = false
  End = (324.937,-1000.03,1701.28)
  FilletRadius = 0
  Length = 1236.1
  MakeFace = true
  MapMode = 5
  Points = (2) [(1051.49,1.3321e-09,1701.28),(324.937,-1000.03,1701.28)]
  Start = (1051.49,1.332e-09,1701.28)
  Subdivisions = 0
FEATURE [Part::Feature] Clone001057  label="strutcap077"
  Placement = pos=(-17.7984,-12.9315,1993.75) rot=(0.300929,-0.926151,0.227346;1.92056rad)
  shape: bbox 31.35 x 28.31 x 22.68 mm, 19 faces (baked)
FEATURE [Part::Feature] Cylinder029  label="Cylinder008"
  Placement = pos=(-17.7984,-12.9315,1993.75) rot=(0.376611,0.739148,-0.558413;3.69599rad)
  shape: bbox 821.2 x 600.3 x 295.8 mm, 3 faces (baked)
FEATURE [Part::Feature] Clone001058  label="Hub-019"
  Placement = pos=(-845.374,-614.211,1690.69) rot=(0.320391,0.016792,-0.947137;2.03872rad)
  shape: bbox 52.89 x 52.48 x 37.22 mm, 28 faces (baked)
FEATURE [Part::Feature] Clone001059  label="strutcap078"
  Placement = pos=(-851.64,-595.214,1701.75) rot=(0.399329,0.656651,0.639801;3.91882rad)
  shape: bbox 20.03 x 30.19 x 20.75 mm, 19 faces (baked)
FEATURE [Part::Feature] Clone001060  label="strutcap079"
  Placement = pos=(-866.78,-606.214,1690.18) rot=(0.055489,0.9504,0.306039;3.98098rad)
  shape: bbox 31.55 x 26.91 x 26.68 mm, 19 faces (baked)
FEATURE [Part::Feature] Clone001061  label="strutcap080"
  Placement = pos=(-832.872,-605.127,1707.53) rot=(0.591556,0.192211,0.783018;3.63986rad)
  shape: bbox 30.27 x 27.49 x 25.37 mm, 19 faces (baked)
FEATURE [Part::Feature] Clone001062  label="strutcap081"
  Placement = pos=(-829.243,-626.041,1701.75) rot=(0.652221,-0.288292,0.701067;3.2457rad)
  shape: bbox 31.36 x 25.86 x 20.72 mm, 19 faces (baked)
FEATURE [Part::Feature] Clone001063  label="strutcap082"
  Placement = pos=(-844.383,-637.041,1690.18) rot=(-0.545652,0.692057,-0.472568;3.4603rad)
  shape: bbox 22.9 x 32.27 x 26.72 mm, 19 faces (baked)
FEATURE [Part::Feature] Clone001064  label="strutcap083"
  Placement = pos=(-863.151,-627.127,1684.4) rot=(-0.306822,0.944288,-0.119077;3.84415rad)
  shape: bbox 29.74 x 26.84 x 29.82 mm, 19 faces (baked)
FEATURE [Part::Feature] Cylinder030  label="Varilla-B-modif-011"
  Placement = pos=(-851.641,-593.624,1701.75) rot=(-1e-06,0.707107,0.707107;3.1416rad)
  shape: bbox 10.01 x 1189 x 10 mm, 3 faces (baked)
FEATURE [Part::Feature] Clone001065  label="strutcap084"
  Placement = pos=(6.79873,-20.9232,1993.75) rot=(0.690296,-0.501521,0.521506;2.41724rad)
  shape: bbox 23.54 x 32.47 x 22.68 mm, 19 faces (baked)
FEATURE [App::DocumentObjectGroup] Group011  label="Clave"
  Group = -> [Clone001004,Clone,Clone001065,Clone001057,Clone001049,Clone001015]
FEATURE [Part::Feature] Cylinder031  label="Cylinder009"
  Placement = pos=(6.79873,-20.9232,1993.75) rot=(-0.125384,0.791599,-0.598038;2.95271rad)
  shape: bbox 320.8 x 962 x 295.8 mm, 3 faces (baked)
FEATURE [Part::Feature] Clone001066  label="Hub-020"
  Placement = pos=(322.923,-993.798,1690.69) rot=(0.482777,0.390952,-0.783634;0.910971rad)
  shape: bbox 55.11 x 51.63 x 37.22 mm, 28 faces (baked)
FEATURE [Part::Feature] Clone001067  label="strutcap085"
  Placement = pos=(318.147,-979.1,1707.53) rot=(-0.46391,-0.638529,-0.614059;1.7382rad)
  shape: bbox 23.11 x 31.33 x 25.37 mm, 19 faces (baked)
FEATURE [Part::Feature] Clone001068  label="strutcap086"
  Placement = pos=(302.919,-993.887,1701.75) rot=(0.077008,-0.937624,-0.339015;1.71438rad)
  shape: bbox 31.95 x 22.93 x 20.75 mm, 19 faces (baked)
FEATURE [Part::Feature] Clone001069  label="strutcap087"
  Placement = pos=(308.702,-1011.68,1690.18) rot=(-0.539571,0.841799,-0.015424;4.17481rad)
  shape: bbox 29.86 x 29.01 x 26.68 mm, 19 faces (baked)
FEATURE [Part::Feature] Clone001070  label="strutcap088"
  Placement = pos=(329.714,-1014.7,1684.4) rot=(0.771869,-0.560786,0.299561;2.713rad)
  shape: bbox 22.65 x 31.16 x 29.82 mm, 19 faces (baked)
FEATURE [Part::Feature] Clone001071  label="strutcap089"
  Placement = pos=(344.942,-999.909,1690.18) rot=(0.846307,-0.244693,0.47317;3.42288rad)
  shape: bbox 32.71 x 20 x 26.83 mm, 19 faces (baked)
FEATURE [Part::Feature] Clone001072  label="strutcap090"
  Placement = pos=(339.159,-982.111,1701.75) rot=(0.781158,0.168237,0.601239;4.08322rad)
  shape: bbox 29.92 x 30.42 x 20.72 mm, 19 faces (baked)
FEATURE [Part::Feature] Cylinder032  label="Varilla-B-modif-012"
  Placement = pos=(301.407,-993.395,1701.75) rot=(-0.456971,0.628958,0.628958;3.99886rad)
  shape: bbox 1134 x 376.9 x 10 mm, 3 faces (baked)
FEATURE [Part::Feature] Cylinder033  label="Varilla-B-modif-013"
  Placement = pos=(1037.92,-20.3126,1701.75) rot=(0.908667,-0.295233,-0.295233;1.66643rad)
  shape: bbox 706.8 x 967.7 x 10 mm, 3 faces (baked)
FEATURE [Part::Part2DObjectPython] Line065  # Draft 2D object (typed FeaturePython)
  ChamferSize = 0
  Closed = false
  End = (1376.39,-999.957,1051.5)
  FilletRadius = 0
  Length = 1236.03
  MakeFace = true
  MapMode = 5
  Points = (2) [(324.937,-1000.03,1701.28),(1376.39,-999.957,1051.5)]
  Start = (324.937,-1000.03,1701.28)
  Subdivisions = 0
FEATURE [Part::Feature] Cylinder034  label="Varilla-B-modif-014"
  Placement = pos=(1357.36,-1000.76,1064.14) rot=(0.086928,-0.983946,-0.155865;1.03106rad)
  shape: bbox 1017 x 10.03 x 633.5 mm, 3 faces (baked)
FEATURE [Part::Feature] Clone001073  label="strutcap091"
  Placement = pos=(1357.54,-999.86,1064.43) rot=(0.250583,-0.868506,-0.427675;1.13881rad)
  shape: bbox 30.96 x 20.1 x 29.71 mm, 19 faces (baked)
FEATURE [Part::Feature] Cylinder035  label="Cylinder010"
  Placement = pos=(329.697,1014.7,1684.4) rot=(0.985873,-0.156147,0.060603;3.87249rad)
  shape: bbox 228.1 x 679.5 x 779.7 mm, 3 faces (baked)
FEATURE [Part::Feature] Cylinder036  label="Varilla-B-modif-015"
  Placement = pos=(1357.49,999.919,1064.43) rot=(-0.245397,-0.863791,0.440052;1.14636rad)
  shape: bbox 1017 x 10.05 x 633.5 mm, 3 faces (baked)
FEATURE [Part::Feature] Cylinder037  label="Varilla-B-modif-016"
  Placement = pos=(307.663,1011.8,1689.56) rot=(0.557122,0.830163,0.021082;4.15722rad)
  shape: bbox 824.6 x 603.3 x 634.3 mm, 3 faces (baked)
FEATURE [Part::Feature] Clone001074  label="strutcap092"
  Placement = pos=(344.925,999.915,1690.18) rot=(0.847741,0.241212,0.472389;2.87537rad)
  shape: bbox 32.7 x 20 x 26.9 mm, 19 faces (baked)
FEATURE [Part::Feature] Clone001075  label="strutcap093"
  Placement = pos=(329.697,1014.7,1684.4) rot=(0.771865,0.560793,0.299559;3.57019rad)
  shape: bbox 22.65 x 31.16 x 29.82 mm, 19 faces (baked)
FEATURE [Part::Feature] Clone001076  label="strutcap094"
  Placement = pos=(308.478,1011.53,1690.32) rot=(0.543251,0.839537,0.007414;4.18045rad)
  shape: bbox 29.9 x 28.94 x 26.61 mm, 19 faces (baked)
FEATURE [Part::Feature] Clone001077  label="strutcap095"
  Placement = pos=(1357.49,999.919,1064.43) rot=(-0.246268,-0.855952,0.454641;1.14624rad)
  shape: bbox 30.92 x 20 x 29.82 mm, 19 faces (baked)
FEATURE [Part::Feature] Cylinder038  label="Varilla-B-modif-017"
  Placement = pos=(-867.207,605.268,1689.56) rot=(-0.035573,0.954465,-0.296196;3.97386rad)
  shape: bbox 825.4 x 602.3 x 634.3 mm, 3 faces (baked)
FEATURE [Part::Feature] Cylinder039  label="Cylinder011"
  Placement = pos=(-863.157,627.12,1684.4) rot=(0.877489,0.447103,-0.173528;3.79809rad)
  shape: bbox 579.9 x 424.4 x 779.7 mm, 3 faces (baked)
FEATURE [Part::Feature] Cylinder040  label="Varilla-B-modif-018"
  Placement = pos=(-531.491,1600.04,1064.43) rot=(0.199138,-0.542979,0.815793;2.00203rad)
  shape: bbox 322.2 x 967.7 x 633.5 mm, 3 faces (baked)
FEATURE [Part::Feature] Cylinder041  label="Varilla-B-modif-019"
  Placement = pos=(-1685.97,-11.0365,1064.43) rot=(0.404604,-0.271467,0.87327;3.07625rad)
  shape: bbox 825.4 x 603.1 x 633.5 mm, 3 faces (baked)
FEATURE [Part::Feature] Cylinder042  label="Cylinder012"
  Placement = pos=(-863.157,-627.12,1684.4) rot=(0.42906,0.842077,-0.326825;3.47161rad)
  shape: bbox 579.9 x 424.4 x 779.7 mm, 3 faces (baked)
FEATURE [Part::Feature] Cylinder043  label="Varilla-B-modif-020"
  Placement = pos=(-843.626,-637.725,1689.56) rot=(-0.547223,0.697036,-0.463345;3.47876rad)
  shape: bbox 321.4 x 967.4 x 634.3 mm, 3 faces (baked)
FEATURE [Part::Feature] Cylinder044  label="Varilla-B-modif-021"
  Placement = pos=(-510.484,-1606.87,1064.43) rot=(0.55703,0.020822,0.830232;4.15797rad)
  shape: bbox 825.4 x 603 x 633.5 mm, 3 faces (baked)
FEATURE [Part::Feature] Cylinder045  label="Cylinder013"
  Placement = pos=(329.705,-1014.7,1684.4) rot=(-0.146074,0.922248,-0.35794;3.02833rad)
  shape: bbox 228.1 x 679.5 x 779.7 mm, 3 faces (baked)
FEATURE [Part::Feature] Cylinder046  label="Cylinder014"
  Placement = pos=(540.281,1707.78,876.414) rot=(0.752998,0.648404,-0.1121;3.71301rad)
  shape: bbox 538.6 x 295.9 x 862.3 mm, 3 faces (baked)
FEATURE [Part::Feature] Cylinder047  label="Cylinder015"
  Placement = pos=(565.816,1699.57,875.771) rot=(0.764557,0.607953,0.214116;2.70375rad)
  shape: bbox 604.8 x 89.65 x 862.6 mm, 3 faces (baked)
FEATURE [Part::Feature] Cylinder048  label="Varilla-B-modif-022"
  Placement = pos=(22.9176,1992.61,-2.89e-13) rot=(0.697446,0.506739,0.506739;1.92357rad)
  shape: bbox 1134 x 376.8 x 10 mm, 3 faces (baked)
FEATURE [Part::Feature] Cylinder049  label="Cylinder016"
  Placement = pos=(-1457.24,1041.57,876.414) rot=(0.221853,0.940826,-0.256178;3.47269rad)
  shape: bbox 445.1 x 424.7 x 862.3 mm, 3 faces (baked)
FEATURE [Part::Feature] Cylinder050  label="Varilla-B-modif-023"
  Placement = pos=(-1888,637.545,-2.89e-13) rot=(0.223909,0.689153,0.689153;2.70104rad)
  shape: bbox 706.8 x 967.7 x 10 mm, 3 faces (baked)
FEATURE [Part::Feature] Cylinder051  label="Cylinder017"
  Placement = pos=(-1441.54,1063.32,875.771) rot=(0.255317,0.92006,0.297158;3.03584rad)
  shape: bbox 269.8 x 551.3 x 862.6 mm, 3 faces (baked)
FEATURE [Part::Feature] Cylinder052  label="Varilla-B-modif-024"
  Placement = pos=(-1189.77,-1598.58,-2.89e-13) rot=(-0.223929,0.68915,0.68915;3.58218rad)
  shape: bbox 706.9 x 967.6 x 10 mm, 3 faces (baked)
FEATURE [Part::Feature] Cylinder053  label="Cylinder018"
  Placement = pos=(-1440.9,-1064.05,876.414) rot=(-0.368456,0.879459,-0.301316;3.11119rad)
  shape: bbox 270.1 x 551.7 x 862.3 mm, 3 faces (baked)
FEATURE [Part::Feature] Cylinder054  label="Cylinder019"
  Placement = pos=(-1456.73,-1042.4,875.771) rot=(-0.336706,0.901009,0.273516;3.40569rad)
  shape: bbox 444.9 x 424.3 x 862.6 mm, 3 faces (baked)
FEATURE [Part::Feature] Cylinder055  label="Cylinder020"
  Placement = pos=(541.239,-1707.55,875.771) rot=(0.824708,-0.546051,-0.147262;2.60334rad)
  shape: bbox 538.1 x 295.8 x 862.6 mm, 3 faces (baked)
FEATURE [Part::Feature] Cylinder056  label="Varilla-B-modif-025"
  Placement = pos=(1152.7,-1625.51,0) rot=(0.69747,-0.506723,-0.506723;1.92354rad)
  shape: bbox 1134 x 376.9 x 10 mm, 3 faces (baked)
FEATURE [Part::Feature] Cylinder057  label="Cylinder021"
  Placement = pos=(566.724,-1699.19,876.414) rot=(0.829948,-0.503984,0.239135;3.52267rad)
  shape: bbox 605.2 x 89.84 x 862.3 mm, 3 faces (baked)
FEATURE [Part::Feature] Clone001078  label="strutcap096"
  Placement = pos=(530.378,1699.18,898.82) rot=(-0.414259,-0.732085,0.540778;1.78299rad)
  shape: bbox 30.96 x 20.14 x 22.38 mm, 19 faces (baked)
FEATURE [Part::Feature] Clone001079  label="strutcap097"
  Placement = pos=(540.273,1707.74,876.408) rot=(0.753174,0.648286,-0.111595;3.71391rad)
  shape: bbox 26.59 x 25.55 x 30.67 mm, 19 faces (baked)
FEATURE [Part::Feature] Clone001080  label="strutcap098"
  Placement = pos=(565.808,1699.53,875.769) rot=(0.764338,0.608049,0.214624;2.70459rad)
  shape: bbox 28.6 x 20 x 30.68 mm, 19 faces (baked)
FEATURE [Part::Feature] Clone001081  label="strutcap099"
  Placement = pos=(570.601,1687.09,896.949) rot=(0.782815,0.102142,0.613814;1.95118rad)
  shape: bbox 32 x 28.57 x 22.88 mm, 19 faces (baked)
FEATURE [Part::Feature] Clone001082  label="strutcap100"
  Placement = pos=(548.01,1686.6,911.365) rot=(0.323892,-0.445799,0.83448;1.43273rad)
  shape: bbox 21.5 x 28.59 x 31.71 mm, 19 faces (baked)
FEATURE [Part::Feature] Clone001083  label="Hub5-01-clave004"
  Placement = pos=(549.337,1690.68,888.915) rot=(0.403006,0.403003,0.82169;3.9346rad)
  shape: bbox 54.11 x 37.29 x 51.33 mm, 25 faces (baked)
FEATURE [Part::Feature] Clone001084  label="Hub5-01-clave005"
  Placement = pos=(-1438.18,1044.9,888.915) rot=(-0.126077,-0.795998,-0.592023;1.42128rad)
  shape: bbox 45.2 x 49.91 x 51.33 mm, 25 faces (baked)
FEATURE [Part::Feature] Clone001085  label="strutcap101"
  Placement = pos=(-1457.21,1041.55,876.408) rot=(0.222054,0.940813,-0.256052;3.47399rad)
  shape: bbox 28.2 x 24.81 x 30.67 mm, 19 faces (baked)
FEATURE [Part::Feature] Clone001086  label="strutcap102"
  Placement = pos=(-1441.51,1063.3,875.769) rot=(0.255103,0.920065,0.297325;3.03711rad)
  shape: bbox 22.21 x 29.03 x 30.68 mm, 19 faces (baked)
FEATURE [Part::Feature] Clone001087  label="strutcap103"
  Placement = pos=(-1428.19,1064.01,896.949) rot=(0.480485,0.454913,0.749792;2.83064rad)
  shape: bbox 30.89 x 29.5 x 22.88 mm, 19 faces (baked)
FEATURE [Part::Feature] Clone001088  label="strutcap104"
  Placement = pos=(-1434.71,1042.38,911.365) rot=(0.359362,-0.116764,0.925865;2.55715rad)
  shape: bbox 27.2 x 24.82 x 31.71 mm, 19 faces (baked)
FEATURE [Part::Feature] Clone001089  label="strutcap105"
  Placement = pos=(-1452.12,1029.49,898.82) rot=(0.076698,-0.673574,0.735129;2.61355rad)
  shape: bbox 25.23 x 31.29 x 22.38 mm, 19 faces (baked)
FEATURE [Part::Feature] Clone001090  label="Hub5-01-clave006"
  Placement = pos=(-1438.18,-1044.9,888.915) rot=(0.440106,-0.863765,0.245392;1.14634rad)
  shape: bbox 45.2 x 49.91 x 51.33 mm, 25 faces (baked)
FEATURE [Part::Feature] Clone001091  label="strutcap106"
  Placement = pos=(-1456.71,-1042.38,875.769) rot=(-0.336923,0.900992,0.273307;3.40693rad)
  shape: bbox 28.13 x 24.8 x 30.68 mm, 19 faces (baked)
FEATURE [Part::Feature] Clone001092  label="strutcap107"
  Placement = pos=(-1453.27,-1029.49,896.949) rot=(0.126083,0.675935,0.726096;3.77224rad)
  shape: bbox 25.11 x 31.29 x 22.88 mm, 19 faces (baked)
FEATURE [Part::Feature] Clone001093  label="strutcap108"
  Placement = pos=(-1434.71,-1042.38,911.365) rot=(0.359362,0.116764,0.925865;3.72603rad)
  shape: bbox 27.2 x 24.82 x 31.71 mm, 19 faces (baked)
FEATURE [Part::Feature] Clone001094  label="strutcap109"
  Placement = pos=(-1427.84,-1062.91,898.82) rot=(0.451787,-0.493106,0.743461;3.55656rad)
  shape: bbox 30.89 x 29.64 x 22.38 mm, 19 faces (baked)
FEATURE [Part::Feature] Clone001095  label="strutcap110"
  Placement = pos=(-1440.88,-1064.03,876.408) rot=(-0.368245,0.879462,-0.301567;3.11241rad)
  shape: bbox 22.22 x 29.51 x 30.67 mm, 19 faces (baked)
FEATURE [Part::Feature] Clone001096  label="Hub5-01-clave007"
  Placement = pos=(549.351,-1690.68,888.915) rot=(0.58635,-0.29876,0.752952;1.85083rad)
  shape: bbox 54.11 x 37.29 x 51.33 mm, 25 faces (baked)
FEATURE [Part::Feature] Clone001097  label="strutcap111"
  Placement = pos=(530.035,-1700.27,896.949) rot=(0.372241,-0.78273,-0.49877;1.70887rad)
  shape: bbox 30.96 x 20.06 x 22.88 mm, 19 faces (baked)
FEATURE [Part::Feature] Clone001098  label="strutcap112"
  Placement = pos=(541.226,-1707.52,875.769) rot=(0.824895,-0.545917,-0.146708;2.60259rad)
  shape: bbox 26.57 x 25.89 x 30.68 mm, 19 faces (baked)
FEATURE [Part::Feature] Clone001099  label="strutcap113"
  Placement = pos=(548.024,-1686.6,911.365) rot=(-0.323892,-0.445802,-0.834479;1.43272rad)
  shape: bbox 21.5 x 28.59 x 31.71 mm, 19 faces (baked)
FEATURE [Part::Feature] Clone001100  label="strutcap114"
  Placement = pos=(569.68,-1686.41,898.82) rot=(-0.797368,0.162279,-0.581265;1.86885rad)
  shape: bbox 32.15 x 28.57 x 22.38 mm, 19 faces (baked)
FEATURE [Part::Feature] Clone001101  label="strutcap115"
  Placement = pos=(566.711,-1699.15,876.408) rot=(0.829728,-0.504084,0.239691;3.52197rad)
  shape: bbox 29.43 x 20.13 x 30.67 mm, 19 faces (baked)
FEATURE [Part::Feature] Clone001102  label="Hub-021"
  Placement = pos=(-522.419,1607.96,1044.94) rot=(-0.404151,-0.556253,-0.726117;1.57141rad)
  shape: bbox 54.14 x 40.13 x 50.11 mm, 28 faces (baked)
FEATURE [Part::Feature] Clone001105  label="strutcap118"
  Placement = pos=(-516.067,1625.93,1032.31) rot=(0.655766,0.705688,0.268283;3.03581rad)
  shape: bbox 25.3 x 25.97 x 30.96 mm, 19 faces (baked)
FEATURE [Part::Feature] Clone001106  label="strutcap119"
  Placement = pos=(-503.124,1619.77,1048.2) rot=(0.67398,0.417938,0.609162;2.53046rad)
  shape: bbox 30.99 x 22.33 x 20.3 mm, 19 faces (baked)
FEATURE [Part::Feature] Clone001107  label="strutcap120"
  Placement = pos=(-510.484,1606.82,1064.4) rot=(0.551632,-0.035834,0.833318;2.11859rad)
  shape: bbox 28.95 x 26.75 x 29.86 mm, 19 faces (baked)
FEATURE [Part::Feature] Clone001108  label="strutcap121"
  Placement = pos=(-531.49,1600.04,1064.43) rot=(0.195018,-0.537301,0.820534;2.01296rad)
  shape: bbox 24.18 x 30.56 x 29.82 mm, 19 faces (baked)
FEATURE [Part::Feature] Clone001109  label="Hub-022"
  Placement = pos=(-1690.7,0.0372864,1044.94) rot=(-1.1e-05,-1,-2e-05;1.01578rad)
  shape: bbox 37.43 x 53.16 x 50.11 mm, 28 faces (baked)
FEATURE [Part::Feature] Clone001111  label="strutcap123"
  Placement = pos=(-1705.82,11.6304,1032.31) rot=(0.116339,0.961371,0.249462;3.3715rad)
  shape: bbox 23.88 x 27.32 x 30.96 mm, 19 faces (baked)
FEATURE [Part::Feature] Clone001112  label="strutcap124"
  Placement = pos=(-1695.97,22.0374,1048.2) rot=(0.287109,0.703654,0.649954;3.33809rad)
  shape: bbox 21.94 x 32.05 x 20.3 mm, 19 faces (baked)
FEATURE [Part::Feature] Clone001113  label="strutcap125"
  Placement = pos=(-1685.93,11.0372,1064.4) rot=(0.407724,0.257586,0.87602;3.20384rad)
  shape: bbox 29.33 x 26.91 x 29.86 mm, 19 faces (baked)
FEATURE [Part::Feature] Clone001114  label="strutcap126"
  Placement = pos=(-1685.97,-11.0364,1064.43) rot=(0.40029,-0.270519,0.87555;3.09124rad)
  shape: bbox 29.19 x 27.26 x 29.82 mm, 19 faces (baked)
FEATURE [Part::Feature] Clone001116  label="Hub-023"
  Placement = pos=(-522.49,-1607.94,1044.94) rot=(0.404145,-0.55627,0.726106;1.57137rad)
  shape: bbox 54.14 x 40.13 x 50.11 mm, 28 faces (baked)
FEATURE [Part::Feature] Clone001117  label="strutcap128"
  Placement = pos=(-510.498,-1606.87,1064.43) rot=(0.555204,0.018892,0.8315;4.17521rad)
  shape: bbox 29.12 x 26.51 x 29.82 mm, 19 faces (baked)
FEATURE [Part::Feature] Clone001118  label="strutcap129"
  Placement = pos=(-531.478,-1600,1064.4) rot=(-0.211892,-0.532008,-0.819798;2.00111rad)
  shape: bbox 23.74 x 30.6 x 29.86 mm, 19 faces (baked)
FEATURE [Part::Feature] Clone001119  label="strutcap130"
  Placement = pos=(-545.042,-1606.15,1048.2) rot=(-0.203171,0.82696,0.52427;4.09656rad)
  shape: bbox 32.67 x 26.78 x 20.3 mm, 19 faces (baked)
FEATURE [Part::Feature] Clone001120  label="strutcap131"
  Placement = pos=(-538.189,-1618.74,1032.31) rot=(-0.481748,0.865531,0.13702;3.62315rad)
  shape: bbox 28.95 x 20.82 x 30.96 mm, 19 faces (baked)
FEATURE [Part::Feature] Cylinder058  label="Cylinder022"
  Placement = pos=(530.378,1699.21,898.834) rot=(-0.413717,-0.732343,0.540844;1.78399rad)
  shape: bbox 1035 x 89.07 x 159.4 mm, 3 faces (baked)
FEATURE [Part::Feature] Cylinder059  label="Cylinder023"
  Placement = pos=(570.617,1687.11,896.969) rot=(0.783276,0.101681,0.613303;1.95105rad)
  shape: bbox 795.2 x 679.7 x 161.3 mm, 3 faces (baked)
FEATURE [Part::Feature] Cylinder060  label="Varilla-B-modif-026"
  Placement = pos=(1372.43,1012.12,1030.9) rot=(0.616123,0.772286,0.154811;3.60091rad)
  shape: bbox 201.9 x 602.9 x 1017 mm, 3 faces (baked)
FEATURE [Part::Feature] Clone001123  label="strutcap134"
  Placement = pos=(1359.16,1014.63,1048.2) rot=(-0.756432,-0.638991,0.139644;1.73831rad)
  shape: bbox 30 x 31.16 x 20.3 mm, 19 faces (baked)
FEATURE [Part::Feature] Clone001124  label="strutcap135"
  Placement = pos=(1373.75,1011.64,1032.01) rot=(0.909322,0.414351,0.038035;3.6661rad)
  shape: bbox 20.28 x 29.06 x 31.05 mm, 19 faces (baked)
FEATURE [Part::Feature] Clone001125  label="Hub-024"
  Placement = pos=(1167.88,1607.21,-5e-15) rot=(-0.413351,0.811346,0.413351;1.77835rad)
  shape: bbox 48.34 x 39.86 x 55.6 mm, 28 faces (baked)
FEATURE [Part::Feature] Clone001126  label="strutcap136"
  Placement = pos=(1162.63,1618.69,19.0526) rot=(-0.354648,-0.474559,0.805617;1.14619rad)
  shape: bbox 28.01 x 22.72 x 31.69 mm, 19 faces (baked)
FEATURE [Part::Feature] Clone001127  label="strutcap137"
  Placement = pos=(1153.73,1625.15,0) rot=(-0.697483,-0.506713,0.506713;1.92352rad)
  shape: bbox 31.34 x 25.98 x 20 mm, 19 faces (baked)
FEATURE [Part::Feature] Clone001128  label="strutcap138"
  Placement = pos=(1180.54,1607.1,19.8831) rot=(0.632762,0.03188,0.77369;0.99253rad)
  shape: bbox 25.27 x 26.79 x 31.62 mm, 19 faces (baked)
FEATURE [Part::Feature] Clone001129  label="strutcap139"
  Placement = pos=(1189.16,1599.52,-2.5e-14) rot=(0.908302,0.295794,0.295794;1.66683rad)
  shape: bbox 30.1 x 30.58 x 20 mm, 19 faces (baked)
FEATURE [Part::Feature] Cylinder061  label="Varilla-B-modif-027"
  Placement = pos=(1189.84,1598.52,-2.89e-13) rot=(0.908667,0.295233,0.295233;1.66643rad)
  shape: bbox 706.8 x 967.7 x 10 mm, 3 faces (baked)
FEATURE [Part::Feature] Cylinder062  label="Varilla-B-modif-028"
  Placement = pos=(-538.473,1618.02,1030.9) rot=(0.045055,0.998909,-0.012317;3.69415rad)
  shape: bbox 633 x 11.04 x 1017 mm, 3 faces (baked)
FEATURE [Part::Feature] Cylinder063  label="Varilla-B-modif-029"
  Placement = pos=(-10.1769,1992.61,20.4541) rot=(0.167218,-0.60597,0.777714;0.899398rad)
  shape: bbox 514.7 x 376.9 x 1017 mm, 3 faces (baked)
FEATURE [Part::Feature] Cylinder064  label="Cylinder024"
  Placement = pos=(-1428.21,1064.04,896.969) rot=(0.481026,0.454827,0.749497;2.83001rad)
  shape: bbox 888.2 x 550.9 x 161.3 mm, 3 faces (baked)
FEATURE [Part::Feature] Clone001130  label="strutcap140"
  Placement = pos=(-544.971,1606.18,1048.2) rot=(0.203272,0.826904,-0.52432;4.09647rad)
  shape: bbox 32.67 x 26.78 x 20.3 mm, 19 faces (baked)
FEATURE [Part::Feature] Clone001131  label="strutcap141"
  Placement = pos=(-537.612,1619.12,1032.01) rot=(0.488533,0.863387,-0.126091;3.6085rad)
  shape: bbox 28.61 x 21.1 x 31.05 mm, 19 faces (baked)
FEATURE [Part::Feature] Cylinder065  label="Cylinder025"
  Placement = pos=(-1453.3,-1029.5,896.969) rot=(0.126564,0.676057,0.725898;3.77131rad)
  shape: bbox 252.7 x 1010 x 161.3 mm, 3 faces (baked)
FEATURE [Part::Feature] Cylinder066  label="Cylinder026"
  Placement = pos=(-1452.15,1029.5,898.834) rot=(0.077196,-0.673675,0.734984;2.61448rad)
  shape: bbox 253.8 x 1010 x 159.4 mm, 3 faces (baked)
FEATURE [Part::Feature] Cylinder067  label="Varilla-B-modif-030"
  Placement = pos=(-1898.23,606.07,20.4541) rot=(0.251906,-0.2009,0.946669;2.02469rad)
  shape: bbox 203 x 603 x 1017 mm, 3 faces (baked)
FEATURE [Part::Feature] Cylinder068  label="Varilla-B-modif-031"
  Placement = pos=(-1705.23,-12.1218,1030.9) rot=(-0.54234,0.821957,-0.173938;3.57234rad)
  shape: bbox 203.8 x 602.3 x 1017 mm, 3 faces (baked)
FEATURE [Part::Feature] Clone001132  label="strutcap142"
  Placement = pos=(-1695.97,-21.9626,1048.2) rot=(-0.287012,0.703678,-0.64997;3.33796rad)
  shape: bbox 21.94 x 32.05 x 20.3 mm, 19 faces (baked)
FEATURE [Part::Feature] Clone001133  label="strutcap143"
  Placement = pos=(-1706.01,-10.9624,1032.01) rot=(-0.109939,0.96532,-0.236791;3.37221rad)
  shape: bbox 24.01 x 26.91 x 31.05 mm, 19 faces (baked)
FEATURE [Part::Feature] Cylinder069  label="Cylinder027"
  Placement = pos=(-1427.84,-1062.95,898.834) rot=(0.452335,-0.492994,0.743203;3.55725rad)
  shape: bbox 887.9 x 551.9 x 159.4 mm, 3 faces (baked)
FEATURE [Part::Feature] Cylinder070  label="Cylinder028"
  Placement = pos=(530.036,-1700.3,896.969) rot=(0.371723,-0.782962,-0.498791;1.70995rad)
  shape: bbox 1035 x 90.15 x 161.3 mm, 3 faces (baked)
FEATURE [Part::Feature] Cylinder071  label="Varilla-B-modif-032"
  Placement = pos=(-515.403,-1625.52,1030.9) rot=(0.903009,-0.3391,0.263791;2.99542rad)
  shape: bbox 513.7 x 377.4 x 1017 mm, 3 faces (baked)
FEATURE [Part::Feature] Cylinder072  label="Varilla-B-modif-033"
  Placement = pos=(-1162.98,-1618.04,20.4541) rot=(0.273237,-0.012278,0.961868;3.22808rad)
  shape: bbox 633.5 x 10.03 x 1017 mm, 3 faces (baked)
FEATURE [Part::Feature] Clone001134  label="strutcap144"
  Placement = pos=(-503.182,-1619.75,1048.2) rot=(0.673934,-0.418028,0.609152;3.75287rad)
  shape: bbox 30.99 x 22.33 x 20.3 mm, 19 faces (baked)
FEATURE [Part::Feature] Clone001135  label="strutcap145"
  Placement = pos=(-516.746,-1625.9,1032.01) rot=(-0.652655,0.712308,-0.258186;3.0512rad)
  shape: bbox 24.88 x 26 x 31.05 mm, 19 faces (baked)
FEATURE [Part::Feature] Cylinder073  label="Cylinder029"
  Placement = pos=(569.712,-1686.43,898.834) rot=(-0.797837,0.161779,-0.580762;1.86862rad)
  shape: bbox 796.1 x 679.1 x 159.4 mm, 3 faces (baked)
FEATURE [Part::Feature] Cylinder074  label="Varilla-B-modif-034"
  Placement = pos=(1179.48,-1606.05,20.4541) rot=(-0.285022,-0.188133,-0.939877;1.85504rad)
  shape: bbox 203 x 603.1 x 1017 mm, 3 faces (baked)
FEATURE [Part::Feature] Clone001136  label="Hub-025"
  Placement = pos=(0.0486416,1986.72,-5e-15) rot=(-0.577341,0.577369,0.577341;2.09437rad)
  shape: bbox 53.16 x 12.4 x 55.6 mm, 28 faces (baked)
FEATURE [Part::Feature] Clone001137  label="strutcap146"
  Placement = pos=(-21.9511,1992.92,0) rot=(0.456975,0.628957,-0.628957;3.99887rad)
  shape: bbox 32.2 x 23.31 x 20 mm, 19 faces (baked)
FEATURE [Part::Feature] Clone001138  label="strutcap147"
  Placement = pos=(-10.9511,1992.92,19.0526) rot=(-0.043067,-0.321506,0.945927;1.61128rad)
  shape: bbox 24.46 x 22.68 x 32.46 mm, 19 faces (baked)
FEATURE [Part::Feature] Clone001139  label="strutcap148"
  Placement = pos=(10.3528,1994.07,19.8831) rot=(0.407648,0.155548,0.899793;1.52684rad)
  shape: bbox 27.6 x 22.68 x 31.62 mm, 19 faces (baked)
FEATURE [Part::Feature] Clone001140  label="strutcap149"
  Placement = pos=(21.7815,1993.01,-2.5e-14) rot=(0.696937,0.507089,0.507089;1.92426rad)
  shape: bbox 32.2 x 23.29 x 20 mm, 19 faces (baked)
FEATURE [Part::Feature] Cylinder075  label="Varilla-B-modif-035"
  Placement = pos=(-1152.6,1625.58,-2.89e-13) rot=(0.456975,0.628957,0.628957;2.28431rad)
  shape: bbox 1134 x 376.9 x 10 mm, 3 faces (baked)
FEATURE [Part::Feature] Clone001141  label="Hub-026"
  Placement = pos=(-1889.47,613.977,-5e-15) rot=(0.702712,-0.111316,-0.702712;3.36331rad)
  shape: bbox 27.47 x 52.09 x 55.6 mm, 28 faces (baked)
FEATURE [Part::Feature] Clone001142  label="strutcap150"
  Placement = pos=(-1898.77,605.432,19.0526) rot=(0.112612,-0.208529,0.971511;2.82156rad)
  shape: bbox 20.37 x 25.38 x 32.46 mm, 19 faces (baked)
FEATURE [Part::Feature] Clone001143  label="strutcap151"
  Placement = pos=(-1902.17,594.971,0) rot=(8e-06,0.707107,-0.707107;3.14161rad)
  shape: bbox 20.3 x 30 x 20 mm, 19 faces (baked)
FEATURE [Part::Feature] Clone001144  label="strutcap152"
  Placement = pos=(-1893.28,626.049,19.8831) rot=(0.168898,0.258947,0.95101;2.70038rad)
  shape: bbox 25.15 x 27.06 x 31.62 mm, 19 faces (baked)
FEATURE [Part::Feature] Clone001145  label="strutcap153"
  Placement = pos=(-1888.73,636.589,-2.5e-14) rot=(0.22342,0.689233,0.689233;2.70197rad)
  shape: bbox 27.81 x 32.24 x 20 mm, 19 faces (baked)
FEATURE [Part::Feature] Clone001146  label="Hub-027"
  Placement = pos=(-1167.76,1607.29,-5e-15) rot=(0.665244,-0.33897,-0.665244;3.79522rad)
  shape: bbox 48.34 x 39.85 x 55.6 mm, 28 faces (baked)
FEATURE [Part::Feature] Clone001147  label="strutcap154"
  Placement = pos=(-1180.31,1605.85,19.0526) rot=(0.047109,-0.257408,0.965154;2.21275rad)
  shape: bbox 22.76 x 25.45 x 32.46 mm, 19 faces (baked)
FEATURE [Part::Feature] Clone001148  label="strutcap155"
  Placement = pos=(-1189.21,1599.38,0) rot=(0.223919,0.689152,-0.689152;3.58216rad)
  shape: bbox 30.09 x 30.59 x 20 mm, 19 faces (baked)
FEATURE [Part::Feature] Clone001149  label="strutcap156"
  Placement = pos=(-1163.75,1619.3,19.8831) rot=(0.270223,0.217936,0.937808;2.10624rad)
  shape: bbox 27.56 x 22.35 x 31.62 mm, 19 faces (baked)
FEATURE [Part::Feature] Clone001150  label="strutcap157"
  Placement = pos=(-1153.87,1625.15,-2.5e-14) rot=(0.456433,0.629154,0.629154;2.28521rad)
  shape: bbox 31.34 x 26 x 20 mm, 19 faces (baked)
FEATURE [Part::Feature] Cylinder076  label="Varilla-B-modif-036"
  Placement = pos=(-1902.18,-593.911,-2.89e-13) rot=(-2e-06,0.707107,0.707107;3.1416rad)
  shape: bbox 10.01 x 1189 x 10 mm, 3 faces (baked)
FEATURE [Part::Feature] Clone001151  label="Hub-028"
  Placement = pos=(-1889.51,-613.843,-5e-15) rot=(-0.702716,-0.111274,0.702716;3.36323rad)
  shape: bbox 27.47 x 52.09 x 55.6 mm, 28 faces (baked)
FEATURE [Part::Feature] Clone001152  label="strutcap158"
  Placement = pos=(-1888.61,-636.682,0) rot=(-0.223903,0.689154,-0.689154;2.70105rad)
  shape: bbox 27.82 x 32.23 x 20 mm, 19 faces (baked)
FEATURE [Part::Feature] Clone001153  label="strutcap159"
  Placement = pos=(-1892.01,-626.22,19.0526) rot=(0.171151,-0.163157,0.971641;3.43228rad)
  shape: bbox 24.41 x 24.08 x 32.46 mm, 19 faces (baked)
FEATURE [Part::Feature] Clone001154  label="strutcap160"
  Placement = pos=(-1899.69,-606.315,19.8831) rot=(0.078906,0.292136,0.953116;3.29902rad)
  shape: bbox 20 x 27.5 x 31.62 mm, 19 faces (baked)
FEATURE [Part::Feature] Clone001155  label="strutcap161"
  Placement = pos=(-1902.21,-595.116,-2.5e-14) rot=(-0.00048,0.707107,0.707107;3.14255rad)
  shape: bbox 20.33 x 30.01 x 20 mm, 19 faces (baked)
FEATURE [Part::Feature] Clone001156  label="Hub-029"
  Placement = pos=(-1167.81,-1607.26,-5e-15) rot=(-0.665251,-0.338942,0.665251;3.79517rad)
  shape: bbox 48.34 x 39.86 x 55.6 mm, 28 faces (baked)
FEATURE [Part::Feature] Clone001157  label="strutcap162"
  Placement = pos=(-1180.46,-1607.15,19.8831) rot=(-0.016336,0.32408,0.945889;3.89619rad)
  shape: bbox 25.27 x 26.79 x 31.62 mm, 19 faces (baked)
FEATURE [Part::Feature] Clone001158  label="strutcap163"
  Placement = pos=(-1189.08,-1599.57,-2.5e-14) rot=(-0.224418,0.689071,0.689071;3.58311rad)
  shape: bbox 30.1 x 30.58 x 20 mm, 19 faces (baked)
FEATURE [Part::Feature] Clone001159  label="strutcap164"
  Placement = pos=(-1162.55,-1618.75,19.0526) rot=(0.234252,-0.112384,0.965658;4.04131rad)
  shape: bbox 25.78 x 20.67 x 32.46 mm, 19 faces (baked)
FEATURE [Part::Feature] Clone001160  label="strutcap165"
  Placement = pos=(-1153.65,-1625.21,0) rot=(-0.456958,0.628963,-0.628963;2.28434rad)
  shape: bbox 31.34 x 25.98 x 20 mm, 19 faces (baked)
FEATURE [Part::Feature] Cylinder077  label="Varilla-B-modif-037"
  Placement = pos=(-22.8736,-1992.61,-2.89e-13) rot=(-0.456985,0.628953,0.628953;3.99889rad)
  shape: bbox 1134 x 376.8 x 10 mm, 3 faces (baked)
FEATURE [Part::Feature] Clone001161  label="Hub-030"
  Placement = pos=(0.0119054,-1986.72,-5e-15) rot=(-0.577354,-0.577343,0.577354;4.18878rad)
  shape: bbox 53.16 x 12.4 x 55.6 mm, 28 faces (baked)
FEATURE [Part::Feature] Clone001162  label="strutcap166"
  Placement = pos=(-10.292,-1994.07,19.8831) rot=(0.137371,-0.359993,-0.922786;1.79868rad)
  shape: bbox 27.6 x 22.68 x 31.62 mm, 19 faces (baked)
FEATURE [Part::Feature] Clone001163  label="strutcap167"
  Placement = pos=(11.0118,-1992.92,19.0526) rot=(-0.317192,0.042484,-0.947409;1.63983rad)
  shape: bbox 24.46 x 22.68 x 32.46 mm, 19 faces (baked)
FEATURE [Part::Feature] Clone001164  label="strutcap168"
  Placement = pos=(22.0118,-1992.92,0) rot=(-0.69746,0.50673,-0.50673;1.92355rad)
  shape: bbox 32.2 x 23.31 x 20 mm, 19 faces (baked)
FEATURE [Part::Feature] Clone001165  label="strutcap169"
  Placement = pos=(-21.7208,-1993.01,-2.5e-14) rot=(-0.457503,0.628765,0.628765;3.99974rad)
  shape: bbox 32.2 x 23.29 x 20 mm, 19 faces (baked)
FEATURE [Part::Feature] Clone001166  label="Hub-031"
  Placement = pos=(1167.8,-1607.27,-5e-15) rot=(0.413386,0.81131,-0.413386;1.77839rad)
  shape: bbox 48.34 x 39.86 x 55.6 mm, 28 faces (baked)
FEATURE [Part::Feature] Clone001167  label="strutcap170"
  Placement = pos=(1163.78,-1619.27,19.8831) rot=(0.326774,-0.405165,-0.85385;1.23636rad)
  shape: bbox 27.56 x 22.35 x 31.62 mm, 19 faces (baked)
FEATURE [Part::Feature] Clone001168  label="strutcap171"
  Placement = pos=(1180.34,-1605.82,19.0526) rot=(-0.455439,-0.083356,-0.886356;1.05951rad)
  shape: bbox 22.76 x 25.45 x 32.46 mm, 19 faces (baked)
FEATURE [Part::Feature] Clone001169  label="strutcap172"
  Placement = pos=(1153.91,-1625.13,-2.5e-14) rot=(0.697993,-0.506363,-0.506363;1.92284rad)
  shape: bbox 31.34 x 26 x 20 mm, 19 faces (baked)
FEATURE [Part::Feature] Clone001170  label="strutcap173"
  Placement = pos=(1189.24,-1599.35,0) rot=(-0.908667,0.295233,-0.295233;1.66643rad)
  shape: bbox 30.09 x 30.59 x 20 mm, 19 faces (baked)
FEATURE [Part::Feature] Cylinder078  label="Varilla-B-modif-038"
  Placement = pos=(1888.01,-637.504,0) rot=(0.908674,-0.295221,-0.295221;1.66642rad)
  shape: bbox 706.8 x 967.7 x 10 mm, 3 faces (baked)
FEATURE [App::DocumentObjectGroup] Group010  label="Estructura"
  Group = -> [Clone031,Clone030,Clone028,Cylinder014,Group011,Clone001005,Clone001006,Clone001010,Cylinder016,Clone002,Clone007,Clone005,Clone008,Clone009,Clone001012,Clone001013,Cylinder017,Clone001007,Clone001014,Clone001009,Clone001008,Cylinder015,Cylinder018,Cylinder020,Cylinder019,Clone001016,Clone001020,Clone001018,Clone001023,Clone001027,Cylinder021,Cylinder022,Clone001031,Clone001030,Clone001033,+181 more]
FEATURE [Part::Part2DObjectPython] Line066  # Draft 2D object (typed FeaturePython)
  ChamferSize = 0
  Closed = false
  End = (324.929,1000.03,1701.28)
  FilletRadius = 0
  Length = 1236.04
  MakeFace = true
  MapMode = 5
  Points = (2) [(1376.39,999.957,1051.5),(324.929,1000.03,1701.28)]
  Start = (1376.39,999.957,1051.5)
  Subdivisions = 0
FEATURE [Part::Part2DObjectPython] Line067  # Draft 2D object (typed FeaturePython)
  ChamferSize = 0
  Closed = false
  End = (1376.39,999.957,1051.5)
  FilletRadius = 0
  Length = 1236.04
  MakeFace = true
  MapMode = 5
  Points = (2) [(324.929,1000.03,1701.28),(1376.39,999.957,1051.5)]
  Start = (324.929,1000.03,1701.28)
  Subdivisions = 0
FEATURE [Part::Part2DObjectPython] Line068  # Draft 2D object (typed FeaturePython)
  ChamferSize = 0
  Closed = false
  End = (552.796,1701.28,894.456)
  FilletRadius = 0
  Length = 1093.08
  MakeFace = true
  MapMode = 5
  Points = (2) [(1376.39,999.957,1051.5),(552.796,1701.28,894.456)]
  Start = (1376.39,999.957,1051.5)
  Subdivisions = 0
FEATURE [Part::Part2DObjectPython] Line069  # Draft 2D object (typed FeaturePython)
  ChamferSize = 0
  Closed = false
  End = (552.796,1701.28,894.456)
  FilletRadius = 0
  Length = 1093
  MakeFace = true
  MapMode = 5
  Points = (2) [(324.929,1000.03,1701.28),(552.796,1701.28,894.456)]
  Start = (324.929,1000.03,1701.28)
  Subdivisions = 0
FEATURE [Part::Part2DObjectPython] Line070  # Draft 2D object (typed FeaturePython)
  ChamferSize = 0
  Closed = false
  End = (-525.738,1618.01,1051.5)
  FilletRadius = 0
  Length = 1093.08
  MakeFace = true
  MapMode = 5
  Points = (2) [(552.796,1701.28,894.456),(-525.738,1618.01,1051.5)]
  Start = (552.796,1701.28,894.456)
  Subdivisions = 0
FEATURE [Part::Part2DObjectPython] Line071  # Draft 2D object (typed FeaturePython)
  ChamferSize = 0
  Closed = false
  End = (324.929,1000.03,1701.28)
  FilletRadius = 0
  Length = 1236.02
  MakeFace = true
  MapMode = 5
  Points = (2) [(-525.738,1618.01,1051.5),(324.929,1000.03,1701.28)]
  Start = (-525.738,1618.01,1051.5)
  Subdivisions = 0
FEATURE [Part::Part2DObjectPython] Line072  # Draft 2D object (typed FeaturePython)
  ChamferSize = 0
  Closed = false
  End = (3.6e-11,2000,0)
  FilletRadius = 0
  Length = 1236.11
  MakeFace = true
  MapMode = 5
  Points = (2) [(-525.738,1618.01,1051.5),(3.56977e-11,2000,0)]
  Start = (-525.738,1618.01,1051.5)
  Subdivisions = 0
FEATURE [Part::Part2DObjectPython] Line073  # Draft 2D object (typed FeaturePython)
  ChamferSize = 0
  Closed = false
  End = (552.796,1701.28,894.456)
  FilletRadius = 0
  Length = 1093.1
  MakeFace = true
  MapMode = 5
  Points = (2) [(3.56977e-11,2000,0),(552.796,1701.28,894.456)]
  Start = (3.6e-11,2000,0)
  Subdivisions = 0
FEATURE [Part::Part2DObjectPython] Line074  # Draft 2D object (typed FeaturePython)
  ChamferSize = 0
  Closed = false
  End = (-525.738,1618.01,1051.5)
  FilletRadius = 0
  Length = 1093.08
  MakeFace = true
  MapMode = 5
  Points = (2) [(552.796,1701.28,894.456),(-525.738,1618.01,1051.5)]
  Start = (552.796,1701.28,894.456)
  Subdivisions = 0
FEATURE [Part::Part2DObjectPython] Line075  # Draft 2D object (typed FeaturePython)
  ChamferSize = 0
  Closed = false
  End = (1175.6,1618.02,0)
  FilletRadius = 0
  Length = 1236.11
  MakeFace = true
  MapMode = 5
  Points = (2) [(1376.39,999.957,1051.5),(1175.6,1618.02,0)]
  Start = (1376.39,999.957,1051.5)
  Subdivisions = 0
FEATURE [Part::Part2DObjectPython] Line076  # Draft 2D object (typed FeaturePython)
  ChamferSize = 0
  Closed = false
  End = (552.796,1701.28,894.456)
  FilletRadius = 0
  Length = 1093.1
  MakeFace = true
  MapMode = 5
  Points = (2) [(1175.6,1618.02,0),(552.796,1701.28,894.456)]
  Start = (1175.6,1618.02,0)
  Subdivisions = 0
FEATURE [Part::Part2DObjectPython] Line077  # Draft 2D object (typed FeaturePython)
  ChamferSize = 0
  Closed = false
  End = (-3.6e-11,2000,0)
  FilletRadius = 0
  Length = 1236.1
  MakeFace = true
  MapMode = 5
  Points = (2) [(1175.6,1618.02,0),(-3.5925e-11,2000,0)]
  Start = (1175.6,1618.02,0)
  Subdivisions = 0
FEATURE [Part::Part2DObjectPython] Line078  # Draft 2D object (typed FeaturePython)
  ChamferSize = 0
  Closed = false
  End = (1175.6,1618.02,0)
  FilletRadius = 0
  Length = 1236.1
  MakeFace = true
  MapMode = 5
  Points = (2) [(1902.16,617.998,0),(1175.6,1618.02,0)]
  Start = (1902.16,617.998,0)
  Subdivisions = 0
FEATURE [Part::Part2DObjectPython] Line079  # Draft 2D object (typed FeaturePython)
  ChamferSize = 0
  Closed = false
  End = (1788.83,-9.65e-10,894.484)
  FilletRadius = 0
  Length = 1092.97
  MakeFace = true
  MapMode = 5
  Points = (2) [(1051.49,1.3321e-09,1701.28),(1788.83,-9.64734e-10,894.484)]
  Start = (1051.49,1.332e-09,1701.28)
  Subdivisions = 0
FEATURE [Part::Part2DObjectPython] Line080  # Draft 2D object (typed FeaturePython)
  ChamferSize = 0
  Closed = false
  End = (1376.39,-999.957,1051.5)
  FilletRadius = 0
  Length = 1093.01
  MakeFace = true
  MapMode = 5
  Points = (2) [(1788.83,-9.64734e-10,894.484),(1376.39,-999.957,1051.5)]
  Start = (1788.83,-9.65e-10,894.484)
  Subdivisions = 0
FEATURE [Part::Part2DObjectPython] Line081  # Draft 2D object (typed FeaturePython)
  ChamferSize = 0
  Closed = false
  End = (1788.83,-9.65e-10,894.484)
  FilletRadius = 0
  Length = 1093.01
  MakeFace = true
  MapMode = 5
  Points = (2) [(1376.39,-999.957,1051.5),(1788.83,-9.64734e-10,894.484)]
  Start = (1376.39,-999.957,1051.5)
  Subdivisions = 0
FEATURE [Part::Part2DObjectPython] Line082  # Draft 2D object (typed FeaturePython)
  ChamferSize = 0
  Closed = false
  End = (1902.16,-617.998,0)
  FilletRadius = 0
  Length = 1093.1
  MakeFace = true
  MapMode = 5
  Points = (2) [(1788.83,-9.64734e-10,894.484),(1902.16,-617.998,0)]
  Start = (1788.83,-9.65e-10,894.484)
  Subdivisions = 0
FEATURE [Part::Part2DObjectPython] Line083  # Draft 2D object (typed FeaturePython)
  ChamferSize = 0
  Closed = false
  End = (1902.16,617.998,0)
  FilletRadius = 0
  Length = 1093.1
  MakeFace = true
  MapMode = 5
  Points = (2) [(1788.83,-9.64734e-10,894.484),(1902.16,617.998,0)]
  Start = (1788.83,-9.65e-10,894.484)
  Subdivisions = 0
FEATURE [Part::Part2DObjectPython] Line084  # Draft 2D object (typed FeaturePython)
  ChamferSize = 0
  Closed = false
  End = (1376.39,999.957,1051.5)
  FilletRadius = 0
  Length = 1093.01
  MakeFace = true
  MapMode = 5
  Points = (2) [(1788.83,-9.64734e-10,894.484),(1376.39,999.957,1051.5)]
  Start = (1788.83,-9.65e-10,894.484)
  Subdivisions = 0
FEATURE [Part::Part2DObjectPython] Line085  # Draft 2D object (typed FeaturePython)
  ChamferSize = 0
  Closed = false
  End = (-525.738,1618.01,1051.5)
  FilletRadius = 0
  Length = 1236.01
  MakeFace = true
  MapMode = 5
  Points = (2) [(-850.675,618.052,1701.28),(-525.738,1618.01,1051.5)]
  Start = (-850.675,618.052,1701.28)
  Subdivisions = 0
FEATURE [Part::Part2DObjectPython] Line086  # Draft 2D object (typed FeaturePython)
  ChamferSize = 0
  Closed = false
  End = (-1175.6,1618.02,0)
  FilletRadius = 0
  Length = 1236.11
  MakeFace = true
  MapMode = 5
  Points = (2) [(-525.738,1618.01,1051.5),(-1175.6,1618.02,0)]
  Start = (-525.738,1618.01,1051.5)
  Subdivisions = 0
FEATURE [Part::Part2DObjectPython] Line087  # Draft 2D object (typed FeaturePython)
  ChamferSize = 0
  Closed = false
  End = (-1175.6,1618.02,0)
  FilletRadius = 0
  Length = 1236.1
  MakeFace = true
  MapMode = 5
  Points = (2) [(3.56977e-11,2000,0),(-1175.6,1618.02,0)]
  Start = (3.6e-11,2000,0)
  Subdivisions = 0
FEATURE [Part::Part2DObjectPython] Line088  # Draft 2D object (typed FeaturePython)
  ChamferSize = 0
  Closed = false
  End = (-1701.28,-1.022e-09,1051.5)
  FilletRadius = 0
  Length = 1236.02
  MakeFace = true
  MapMode = 5
  Points = (2) [(-850.675,618.052,1701.28),(-1701.28,-1.02242e-09,1051.5)]
  Start = (-850.675,618.052,1701.28)
  Subdivisions = 0
FEATURE [Part::Part2DObjectPython] Line089  # Draft 2D object (typed FeaturePython)
  ChamferSize = 0
  Closed = false
  End = (-1175.6,1618.02,0)
  FilletRadius = 0
  Length = 1236.1
  MakeFace = true
  MapMode = 5
  Points = (2) [(-1902.16,617.998,0),(-1175.6,1618.02,0)]
  Start = (-1902.16,617.998,0)
  Subdivisions = 0
FEATURE [Part::Part2DObjectPython] Line090  # Draft 2D object (typed FeaturePython)
  ChamferSize = 0
  Closed = false
  End = (-1447.21,1051.46,894.426)
  FilletRadius = 0
  Length = 1093.05
  MakeFace = true
  MapMode = 5
  Points = (2) [(-525.738,1618.01,1051.5),(-1447.21,1051.46,894.426)]
  Start = (-525.738,1618.01,1051.5)
  Subdivisions = 0
FEATURE [Part::Part2DObjectPython] Line091  # Draft 2D object (typed FeaturePython)
  ChamferSize = 0
  Closed = false
  End = (-1175.6,1618.02,0)
  FilletRadius = 0
  Length = 1093.05
  MakeFace = true
  MapMode = 5
  Points = (2) [(-1447.21,1051.46,894.426),(-1175.6,1618.02,0)]
  Start = (-1447.21,1051.46,894.426)
  Subdivisions = 0
FEATURE [Part::Part2DObjectPython] Line092  # Draft 2D object (typed FeaturePython)
  ChamferSize = 0
  Closed = false
  End = (-1902.16,617.998,0)
  FilletRadius = 0
  Length = 1093.1
  MakeFace = true
  MapMode = 5
  Points = (2) [(-1447.21,1051.46,894.426),(-1902.16,617.998,0)]
  Start = (-1447.21,1051.46,894.426)
  Subdivisions = 0
FEATURE [Part::Part2DObjectPython] Line093  # Draft 2D object (typed FeaturePython)
  ChamferSize = 0
  Closed = false
  End = (-1701.28,-1.022e-09,1051.5)
  FilletRadius = 0
  Length = 1093.07
  MakeFace = true
  MapMode = 5
  Points = (2) [(-1447.21,1051.46,894.426),(-1701.28,-1.02242e-09,1051.5)]
  Start = (-1447.21,1051.46,894.426)
  Subdivisions = 0
FEATURE [Part::Part2DObjectPython] Line094  # Draft 2D object (typed FeaturePython)
  ChamferSize = 0
  Closed = false
  End = (-850.675,618.052,1701.28)
  FilletRadius = 0
  Length = 1093.03
  MakeFace = true
  MapMode = 5
  Points = (2) [(-1447.21,1051.46,894.426),(-850.675,618.052,1701.28)]
  Start = (-1447.21,1051.46,894.426)
  Subdivisions = 0
FEATURE [Part::Part2DObjectPython] Line095  # Draft 2D object (typed FeaturePython)
  ChamferSize = 0
  Closed = false
  End = (-850.675,618.052,1701.28)
  FilletRadius = 0
  Length = 1236.1
  MakeFace = true
  MapMode = 5
  Points = (2) [(324.929,1000.03,1701.28),(-850.675,618.052,1701.28)]
  Start = (324.929,1000.03,1701.28)
  Subdivisions = 0
FEATURE [Part::Part2DObjectPython] Line096  # Draft 2D object (typed FeaturePython)
  ChamferSize = 0
  Closed = false
  End = (-1902.16,617.998,0)
  FilletRadius = 0
  Length = 1236.09
  MakeFace = true
  MapMode = 5
  Points = (2) [(-1701.28,-1.02242e-09,1051.5),(-1902.16,617.998,0)]
  Start = (-1701.28,-1.022e-09,1051.5)
  Subdivisions = 0
FEATURE [Part::Part2DObjectPython] Line097  # Draft 2D object (typed FeaturePython)
  ChamferSize = 0
  Closed = false
  End = (1175.6,-1618.02,0)
  FilletRadius = 0
  Length = 1236.11
  MakeFace = true
  MapMode = 5
  Points = (2) [(1376.39,-999.957,1051.5),(1175.6,-1618.02,0)]
  Start = (1376.39,-999.957,1051.5)
  Subdivisions = 0
FEATURE [Part::Part2DObjectPython] Line098  # Draft 2D object (typed FeaturePython)
  ChamferSize = 0
  Closed = false
  End = (552.796,-1701.28,894.456)
  FilletRadius = 0
  Length = 1093.1
  MakeFace = true
  MapMode = 5
  Points = (2) [(1175.6,-1618.02,0),(552.796,-1701.28,894.456)]
  Start = (1175.6,-1618.02,0)
  Subdivisions = 0
FEATURE [Part::Part2DObjectPython] Line099  # Draft 2D object (typed FeaturePython)
  ChamferSize = 0
  Closed = false
  End = (1376.39,-999.957,1051.5)
  FilletRadius = 0
  Length = 1093.08
  MakeFace = true
  MapMode = 5
  Points = (2) [(552.796,-1701.28,894.456),(1376.39,-999.957,1051.5)]
  Start = (552.796,-1701.28,894.456)
  Subdivisions = 0
FEATURE [Part::Part2DObjectPython] Line100  # Draft 2D object (typed FeaturePython)
  ChamferSize = 0
  Closed = false
  End = (324.937,-1000.03,1701.28)
  FilletRadius = 0
  Length = 1093
  MakeFace = true
  MapMode = 5
  Points = (2) [(552.796,-1701.28,894.456),(324.937,-1000.03,1701.28)]
  Start = (552.796,-1701.28,894.456)
  Subdivisions = 0
FEATURE [Part::Part2DObjectPython] Line101  # Draft 2D object (typed FeaturePython)
  ChamferSize = 0
  Closed = false
  End = (-525.738,-1618.01,1051.5)
  FilletRadius = 0
  Length = 1236.03
  MakeFace = true
  MapMode = 5
  Points = (2) [(324.937,-1000.03,1701.28),(-525.738,-1618.01,1051.5)]
  Start = (324.937,-1000.03,1701.28)
  Subdivisions = 0
FEATURE [Part::Part2DObjectPython] Line102  # Draft 2D object (typed FeaturePython)
  ChamferSize = 0
  Closed = false
  End = (552.796,-1701.28,894.456)
  FilletRadius = 0
  Length = 1093.08
  MakeFace = true
  MapMode = 5
  Points = (2) [(-525.738,-1618.01,1051.5),(552.796,-1701.28,894.456)]
  Start = (-525.738,-1618.01,1051.5)
  Subdivisions = 0
FEATURE [Part::Part2DObjectPython] Line103  # Draft 2D object (typed FeaturePython)
  ChamferSize = 0
  Closed = false
  End = (-3.6e-11,-2000,0)
  FilletRadius = 0
  Length = 1093.1
  MakeFace = true
  MapMode = 5
  Points = (2) [(552.796,-1701.28,894.456),(-3.5925e-11,-2000,0)]
  Start = (552.796,-1701.28,894.456)
  Subdivisions = 0
FEATURE [Part::Part2DObjectPython] Line104  # Draft 2D object (typed FeaturePython)
  ChamferSize = 0
  Closed = false
  End = (1175.6,-1618.02,0)
  FilletRadius = 0
  Length = 1236.1
  MakeFace = true
  MapMode = 5
  Points = (2) [(-3.5925e-11,-2000,0),(1175.6,-1618.02,0)]
  Start = (-3.6e-11,-2000,0)
  Subdivisions = 0
FEATURE [Part::Part2DObjectPython] Line105  # Draft 2D object (typed FeaturePython)
  ChamferSize = 0
  Closed = false
  End = (-525.738,-1618.01,1051.5)
  FilletRadius = 0
  Length = 1236.11
  MakeFace = true
  MapMode = 5
  Points = (2) [(-3.5925e-11,-2000,0),(-525.738,-1618.01,1051.5)]
  Start = (-3.6e-11,-2000,0)
  Subdivisions = 0
FEATURE [Part::Part2DObjectPython] Line106  # Draft 2D object (typed FeaturePython)
  ChamferSize = 0
  Closed = false
  End = (-850.675,-618.052,1701.28)
  FilletRadius = 0
  Length = 1236.02
  MakeFace = true
  MapMode = 5
  Points = (2) [(-1701.28,-1.02242e-09,1051.5),(-850.675,-618.052,1701.28)]
  Start = (-1701.28,-1.022e-09,1051.5)
  Subdivisions = 0
FEATURE [Part::Part2DObjectPython] Line107  # Draft 2D object (typed FeaturePython)
  ChamferSize = 0
  Closed = false
  End = (-1902.16,-617.998,0)
  FilletRadius = 0
  Length = 1236.09
  MakeFace = true
  MapMode = 5
  Points = (2) [(-1701.28,-1.02242e-09,1051.5),(-1902.16,-617.998,0)]
  Start = (-1701.28,-1.022e-09,1051.5)
  Subdivisions = 0
FEATURE [Part::Part2DObjectPython] Line108  # Draft 2D object (typed FeaturePython)
  ChamferSize = 0
  Closed = false
  End = (-1902.16,617.998,0)
  FilletRadius = 0
  Length = 1236
  MakeFace = true
  MapMode = 5
  Points = (2) [(-1902.16,-617.998,0),(-1902.16,617.998,0)]
  Start = (-1902.16,-617.998,0)
  Subdivisions = 0
FEATURE [Part::Part2DObjectPython] Line109  # Draft 2D object (typed FeaturePython)
  ChamferSize = 0
  Closed = false
  End = (-525.738,-1618.01,1051.5)
  FilletRadius = 0
  Length = 1236.01
  MakeFace = true
  MapMode = 5
  Points = (2) [(-850.675,-618.052,1701.28),(-525.738,-1618.01,1051.5)]
  Start = (-850.675,-618.052,1701.28)
  Subdivisions = 0
FEATURE [Part::Part2DObjectPython] Line110  # Draft 2D object (typed FeaturePython)
  ChamferSize = 0
  Closed = false
  End = (-1175.6,-1618.02,0)
  FilletRadius = 0
  Length = 1236.11
  MakeFace = true
  MapMode = 5
  Points = (2) [(-525.738,-1618.01,1051.5),(-1175.6,-1618.02,0)]
  Start = (-525.738,-1618.01,1051.5)
  Subdivisions = 0
FEATURE [Part::Part2DObjectPython] Line111  # Draft 2D object (typed FeaturePython)
  ChamferSize = 0
  Closed = false
  End = (-1902.16,-617.998,0)
  FilletRadius = 0
  Length = 1236.1
  MakeFace = true
  MapMode = 5
  Points = (2) [(-1175.6,-1618.02,0),(-1902.16,-617.998,0)]
  Start = (-1175.6,-1618.02,0)
  Subdivisions = 0
FEATURE [Part::Part2DObjectPython] Line112  # Draft 2D object (typed FeaturePython)
  ChamferSize = 0
  Closed = false
  End = (-1447.19,-1051.45,894.481)
  FilletRadius = 0
  Length = 1093.15
  MakeFace = true
  MapMode = 5
  Points = (2) [(-1902.16,-617.998,0),(-1447.19,-1051.45,894.481)]
  Start = (-1902.16,-617.998,0)
  Subdivisions = 0
FEATURE [Part::Part2DObjectPython] Line113  # Draft 2D object (typed FeaturePython)
  ChamferSize = 0
  Closed = false
  End = (-1701.28,-1.022e-09,1051.5)
  FilletRadius = 0
  Length = 1093.05
  MakeFace = true
  MapMode = 5
  Points = (2) [(-1447.19,-1051.45,894.481),(-1701.28,-1.02242e-09,1051.5)]
  Start = (-1447.19,-1051.45,894.481)
  Subdivisions = 0
FEATURE [Part::Part2DObjectPython] Line114  # Draft 2D object (typed FeaturePython)
  ChamferSize = 0
  Closed = false
  End = (-850.675,-618.052,1701.28)
  FilletRadius = 0
  Length = 1092.97
  MakeFace = true
  MapMode = 5
  Points = (2) [(-1447.19,-1051.45,894.481),(-850.675,-618.052,1701.28)]
  Start = (-1447.19,-1051.45,894.481)
  Subdivisions = 0
FEATURE [Part::Part2DObjectPython] Line115  # Draft 2D object (typed FeaturePython)
  ChamferSize = 0
  Closed = false
  End = (-525.738,-1618.01,1051.5)
  FilletRadius = 0
  Length = 1093.03
  MakeFace = true
  MapMode = 5
  Points = (2) [(-1447.19,-1051.45,894.481),(-525.738,-1618.01,1051.5)]
  Start = (-1447.19,-1051.45,894.481)
  Subdivisions = 0
FEATURE [Part::Part2DObjectPython] Line116  # Draft 2D object (typed FeaturePython)
  ChamferSize = 0
  Closed = false
  End = (-1175.6,-1618.02,0)
  FilletRadius = 0
  Length = 1093.1
  MakeFace = true
  MapMode = 5
  Points = (2) [(-1447.19,-1051.45,894.481),(-1175.6,-1618.02,0)]
  Start = (-1447.19,-1051.45,894.481)
  Subdivisions = 0
FEATURE [Part::Part2DObjectPython] Line117  # Draft 2D object (typed FeaturePython)
  ChamferSize = 0
  Closed = false
  End = (-3.6e-11,-2000,0)
  FilletRadius = 0
  Length = 1236.1
  MakeFace = true
  MapMode = 5
  Points = (2) [(-1175.6,-1618.02,0),(-3.5925e-11,-2000,0)]
  Start = (-1175.6,-1618.02,0)
  Subdivisions = 0
FEATURE [Part::Part2DObjectPython] Line118  # Draft 2D object (typed FeaturePython)
  ChamferSize = 0
  Closed = false
  End = (-850.675,618.052,1701.28)
  FilletRadius = 0
  Length = 1093.1
  MakeFace = true
  MapMode = 5
  Points = (2) [(-1.99876e-10,3.00061e-10,2000),(-850.675,618.052,1701.28)]
  Start = (-2e-10,3e-10,2000)
  Subdivisions = 0
FEATURE [Part::Part2DObjectPython] Line119  # Draft 2D object (typed FeaturePython)
  ChamferSize = 0
  Closed = false
  End = (-850.675,-618.052,1701.28)
  FilletRadius = 0
  Length = 1093.1
  MakeFace = true
  MapMode = 5
  Points = (2) [(-1.99876e-10,3.00061e-10,2000),(-850.675,-618.052,1701.28)]
  Start = (-2e-10,3e-10,2000)
  Subdivisions = 0
FEATURE [Part::Part2DObjectPython] Line120  # Draft 2D object (typed FeaturePython)
  ChamferSize = 0
  Closed = false
  End = (324.937,-1000.03,1701.28)
  FilletRadius = 0
  Length = 1093.1
  MakeFace = true
  MapMode = 5
  Points = (2) [(-1.99876e-10,3.00061e-10,2000),(324.937,-1000.03,1701.28)]
  Start = (-2e-10,3e-10,2000)
  Subdivisions = 0
FEATURE [Part::Part2DObjectPython] Line121  # Draft 2D object (typed FeaturePython)
  ChamferSize = 0
  Closed = false
  End = (1051.49,1.332e-09,1701.28)
  FilletRadius = 0
  Length = 1093.1
  MakeFace = true
  MapMode = 5
  Points = (2) [(-1.99876e-10,3.00061e-10,2000),(1051.49,1.3321e-09,1701.28)]
  Start = (-2e-10,3e-10,2000)
  Subdivisions = 0
FEATURE [Part::Part2DObjectPython] Line122  # Draft 2D object (typed FeaturePython)
  ChamferSize = 0
  Closed = false
  End = (324.929,1000.03,1701.28)
  FilletRadius = 0
  Length = 1093.1
  MakeFace = true
  MapMode = 5
  Points = (2) [(-1.99876e-10,3.00061e-10,2000),(324.929,1000.03,1701.28)]
  Start = (-2e-10,3e-10,2000)
  Subdivisions = 0
FEATURE [App::DocumentObjectGroup] Group013  label="Domo-alambrico"
  Group = -> [Line054,Line055,Line056,Line057,Line058,Line059,Line060,Line061,Line062,Line063,Line064,Line065,Line066,Line067,Line068,Line069,Line070,Line071,Line072,Line073,Line074,Line075,Line076,Line077,Line078,Line079,Line080,Line081,Line082,Line083,Line084,Line085,Line086,Line087,Line088,Line089,Line090,Line091,Line092,Line093,Line094,Line095,Line096,Line097,Line098,Line099,Line100,Line101,Line102,Line103,+19 more]
FEATURE [App::Annotation] Text  label="Texto-Material"
  LabelText = Material
  Position = (3227.54,1318.45,0)
FEATURE [App::FeaturePython] Dimension002  # Draft dimension (typed FeaturePython)
  Dimline = (-3.6e-11,-2000,0)
  Direction = (0,0,0)
  Distance = 4000
  End = (-3.6e-11,-2000,0)
  Normal = (0,0,1)
  Start = (-3.6e-11,2000,0)
FEATURE [App::FeaturePython] Dimension003  # Draft dimension (typed FeaturePython)
  Dimline = (-2e-10,3e-10,0)
  Direction = (0,0,0)
  Distance = 2000
  End = (-2e-10,3e-10,0)
  Normal = (0,-1,0)
  Start = (-2e-10,3e-10,2000)
FEATURE [App::FeaturePython] Dimension004  # Draft dimension (typed FeaturePython)
  Dimline = (2000,-600,0)
  Direction = (0,0,0)
  Distance = 1236
  End = (1902.16,-617.998,0)
  Normal = (0,0,1)
  Start = (1902.16,617.998,0)
FEATURE [App::FeaturePython] Dimension005  # Draft dimension (typed FeaturePython)
  Dimline = (1692.93,0,1177.36)
  Direction = (0,0,0)
  Distance = 1092.97
  End = (1788.83,-9.65e-10,894.484)
  Normal = (0,-1,0)
  Start = (1051.49,1.332e-09,1701.28)
FEATURE [App::DocumentObjectGroup] Group014  label="Dimensions"
  Group = -> [Dimension002,Dimension003,Dimension004,Dimension005]
FEATURE [Part::Feature] Cylinder079  label="Varilla-B-modif-039"
  Placement = pos=(3067.05,988.83,0) rot=(1,1.4e-05,1.4e-05;1.5708rad)
  shape: bbox 10.03 x 1189 x 10 mm, 3 faces (baked)
FEATURE [Part::Feature] Cylinder081  label="Cylinder078"
  Placement = pos=(2871.13,-200,5.93e-10) rot=(-1,0,0;1.5708rad)
  shape: bbox 10 x 1047 x 10 mm, 3 faces (baked)
FEATURE [App::Annotation] Text002  label="Texto-varillas"
  LabelText = Varillas
  Position = (2851.65,1075.67,0)
FEATURE [App::Annotation] Text006  label="Texto-varilla-B"
  LabelText = B
  Position = (3045.54,-293.166,0)
FEATURE [App::Annotation] Text007  label="Texto-varilla-A"
  LabelText = A
  Position = (2839.02,-294.635,0)
FEATURE [Part::Feature] Clone001171  label="Hub5-01-clave008"
  Placement = pos=(3486.66,751.241,9.4e-14) rot=(0,0,-1;0.314151rad)
  shape: bbox 54.38 x 55.6 x 12.4 mm, 25 faces (baked)
FEATURE [Part::Feature] Clone001172  label="Hub-032"
  Placement = pos=(3822.07,752.602,-9.09e-13) rot=(0,0,1;0.523599rad)
  shape: bbox 53.16 x 55.6 x 12.4 mm, 28 faces (baked)
FEATURE [App::Annotation] Text008  label="Texto-Piezas-impresas"
  LabelText = Piezas impresas 3D
  Position = (3335.62,1068.59,0)
FEATURE [App::Annotation] Text009  label="Texto-conector-pentagonal"
  LabelText = Conector | pentagonal
  Position = (3357.25,917.695,0)
FEATURE [App::Annotation] Text010  label="Texto-conector-hexagonal"
  LabelText = Conector | Hexagonal
  Position = (3702.82,917.695,0)
FEATURE [Part::Feature] Clone001176  label="strutcap177"
  Placement = pos=(3662.75,464.083,20) rot=(1,0,0;3.14159rad)
  shape: bbox 20.3 x 20 x 30 mm, 19 faces (baked)
FEATURE [App::Annotation] Text012  label="Texto-varillas005"
  LabelText = Teton
  Position = (3595.02,530.248,0)
FEATURE [Part::Feature] Chamfer002  label="Tuerca-M3"
  Placement = pos=(3453.75,-347.288,0) rot=(1,0,0;1.5708rad)
  shape: bbox 6.35 x 6.35 x 2.4 mm, 29 faces (baked)
FEATURE [Part::Feature] Part__Feature002  label="Tornillo-M3"
  Placement = pos=(3442.59,-46.9489,3) rot=(0,-1,0;1.5708rad)
  shape: bbox 13 x 5.5 x 5.5 mm, 16 faces (baked)
FEATURE [App::Annotation] Text017  label="Texto-x30"
  LabelText = x30
  Position = (2840.67,-387.052,0)
FEATURE [App::Annotation] Text019  label="Texto-x35"
  LabelText = x35
  Position = (3032.11,-387.052,0)
FEATURE [App::Annotation] Text020
  LabelText = Tuercas M3
  Position = (3378.67,-274.428,0)
FEATURE [App::Annotation] Text021
  LabelText = Tornillos M3 x 10mm
  Position = (3372,13.5051,0)
FEATURE [App::Annotation] Text022  label="Texto-x6"
  LabelText = x6
  Position = (3441.07,635.345,0)
FEATURE [App::Annotation] Text023  label="Texto-x20"
  LabelText = x20
  Position = (3785.21,635.345,0)
FEATURE [App::Annotation] Text024  label="Texto-x037"
  LabelText = x160
  Position = (3595.42,372.947,0)
FEATURE [Part::Part2DObjectPython] Rectangle  # Draft 2D object (typed FeaturePython)
  ChamferSize = 0
  Columns = 1
  FilletRadius = 0
  Height = -869.038
  Length = 778.826
  MakeFace = false
  MapMode = 5
  Placement = pos=(3282.79,1174.01,0) rot=(0,0,1;0rad)
  Rows = 1
FEATURE [App::Annotation] Text026  label="Texto-Piezas-impresas002"
  LabelText = Tornilleria
  Position = (3493.63,154.878,0)
FEATURE [Part::Part2DObjectPython] Rectangle003  # Draft 2D object (typed FeaturePython)
  ChamferSize = 0
  Columns = 1
  FilletRadius = 0
  Height = -237.557
  Length = 1305.06
  MakeFace = false
  MapMode = 5
  Placement = pos=(2748.42,1457.07,0) rot=(0,0,1;0rad)
  Rows = 1
FEATURE [App::DocumentObjectGroup] Group017  label="Piezas-impresas"
  Group = -> [Clone001171,Clone001172,Clone001176,Text008,Text022,Text023,Text024,Rectangle,Text009,Text010,Text012]
FEATURE [App::Annotation] Text027  label="Texto-x130"
  LabelText = x130
  Position = (3503.66,-74.9347,0)
FEATURE [App::Annotation] Text028  label="Texto-x131"
  LabelText = x130
  Position = (3509.07,-372.19,0)
FEATURE [Part::Part2DObjectPython] Rectangle004  # Draft 2D object (typed FeaturePython)
  ChamferSize = 0
  Columns = 1
  FilletRadius = 0
  Height = -688.616
  Length = 787.849
  MakeFace = false
  MapMode = 5
  Placement = pos=(3285.28,239.952,0) rot=(0,0,1;0rad)
  Rows = 1
FEATURE [App::DocumentObjectGroup] Group018  label="Tornilleria"
  Group = -> [Text026,Text020,Text021,Part__Feature002,Chamfer002,Text027,Text028,Rectangle004]
FEATURE [Part::Part2DObjectPython] Rectangle005  # Draft 2D object (typed FeaturePython)
  ChamferSize = 0
  Columns = 1
  FilletRadius = 0
  Height = -1623.39
  Length = 466.45
  MakeFace = false
  MapMode = 5
  Placement = pos=(2751.78,1169.58,0) rot=(0,0,1;0rad)
  Rows = 1
FEATURE [App::DocumentObjectGroup] Group016  label="Varillas"
  Group = -> [Cylinder079,Cylinder081,Text002,Text006,Text007,Text017,Text019,Rectangle005]
FEATURE [App::DocumentObjectGroup] Group015  label="Materiales"
  Group = -> [Group016,Text,Group017,Group018,Rectangle003]
FEATURE [Part::Feature] Clone001177  label="strutcap178"
  Placement = pos=(-20,-1.7017e-11,-9.6998e-11) rot=(0.707107,0,0.707107;3.14159rad)
  shape: bbox 30 x 20 x 20.3 mm, 19 faces (baked)
FEATURE [Part::Feature] Part__Feature  label="Tornillo-M004"
  Placement = pos=(-5.55,-1.70132e-11,29.9) rot=(0,0,1;0rad)
  shape: bbox 5.5 x 5.5 x 13 mm, 16 faces (baked)
FEATURE [Part::Feature] Chamfer  label="Tuerca-M004"
  Placement = pos=(9.45,-1.7019e-11,6.96667) rot=(1,0,0;1.5708rad)
  shape: bbox 6.35 x 6.35 x 2.4 mm, 29 faces (baked)
FEATURE [Part::Feature] Cylinder082  label="Varilla-B-modif-040"
  Placement = pos=(16.0356,-0.0024909,5.5791e-06) rot=(0.57734,0.577355,0.577355;2.09441rad)
  shape: bbox 1189 x 10.03 x 10 mm, 3 faces (baked)
FEATURE [Part::Part2DObjectPython] Line124  # Draft 2D object (typed FeaturePython)
  ChamferSize = 0
  Closed = false
  End = (-5.55,-1.7e-11,6.56667)
  FilletRadius = 0
  Length = 2.8
  MakeFace = true
  MapMode = 5
  Points = (2) [(-5.55,-1.70175e-11,9.36667),(-5.55,-1.70176e-11,6.56667)]
  Start = (-5.55,-1.7e-11,9.36667)
  Subdivisions = 0
  Support = -> [Clone001177]
FEATURE [Part::Part2DObjectPython] Line125  # Draft 2D object (typed FeaturePython)
  ChamferSize = 0
  Closed = false
  End = (6.7,-1.7e-11,8.16667)
  FilletRadius = 0
  Length = 12.2516
  MakeFace = true
  MapMode = 5
  Points = (2) [(-5.55,-1.70176e-11,7.96667),(6.7,-1.70192e-11,8.16667)]
  Start = (-5.55,-1.7e-11,7.96667)
  Subdivisions = 0
FEATURE [Part::Part2DObjectPython] Line126  # Draft 2D object (typed FeaturePython)
  ChamferSize = 0
  Closed = false
  End = (-5.55,-1.7e-11,7.96667)
  FilletRadius = 0
  Length = 11.9333
  MakeFace = true
  MapMode = 5
  Points = (2) [(-5.55,-1.70177e-11,19.9),(-5.55,-1.70176e-11,7.96667)]
  Start = (-5.55,-1.7e-11,19.9)
  Subdivisions = 0
FEATURE [Part::Part2DObjectPython] Line127  # Draft 2D object (typed FeaturePython)
  ChamferSize = 0
  Closed = false
  End = (-5.55,-1.7e-11,6.56667)
  FilletRadius = 0
  Length = 1.6
  MakeFace = true
  MapMode = 5
  Points = (2) [(-5.55,-1.6,6.56667),(-5.55,-1.70176e-11,6.56667)]
  Start = (-5.55,-1.6,6.56667)
  Subdivisions = 0
FEATURE [App::DocumentObjectGroup] Group020  label="Despiece"
  Group = -> [Clone001177,Part__Feature,Chamfer,Cylinder082,Line124,Line125,Line126,Line127]
FEATURE [Part::Feature] Clone001178  label="strutcap179"
  Placement = pos=(-20,31.6617,-9.6998e-11) rot=(0.707107,0,0.707107;3.14159rad)
  shape: bbox 30 x 20 x 20.3 mm, 19 faces (baked)
FEATURE [Part::Feature] Part__Feature003  label="Tornillo-M005"
  Placement = pos=(-5.55,31.6617,11.9) rot=(0,0,1;0rad)
  shape: bbox 5.5 x 5.5 x 13 mm, 16 faces (baked)
FEATURE [Part::Feature] Chamfer003  label="Tuerca-M005"
  Placement = pos=(-5.55,31.6617,6.96667) rot=(1,0,0;1.5708rad)
  shape: bbox 6.35 x 6.35 x 2.4 mm, 29 faces (baked)
FEATURE [Part::Feature] Cylinder083  label="Varilla-B-modif-041"
  Placement = pos=(-20,31.6617,5.5791e-06) rot=(0.57734,0.577355,0.577355;2.09441rad)
  shape: bbox 1189 x 10.03 x 10 mm, 3 faces (baked)
FEATURE [App::DocumentObjectGroup] Group021  label="Ensamblaje"
  Group = -> [Clone001178,Part__Feature003,Chamfer003,Cylinder083]
FEATURE [App::DocumentObjectGroup] Group019  label="Ensamblaje-tetones"
  Group = -> [Group020,Group021]
